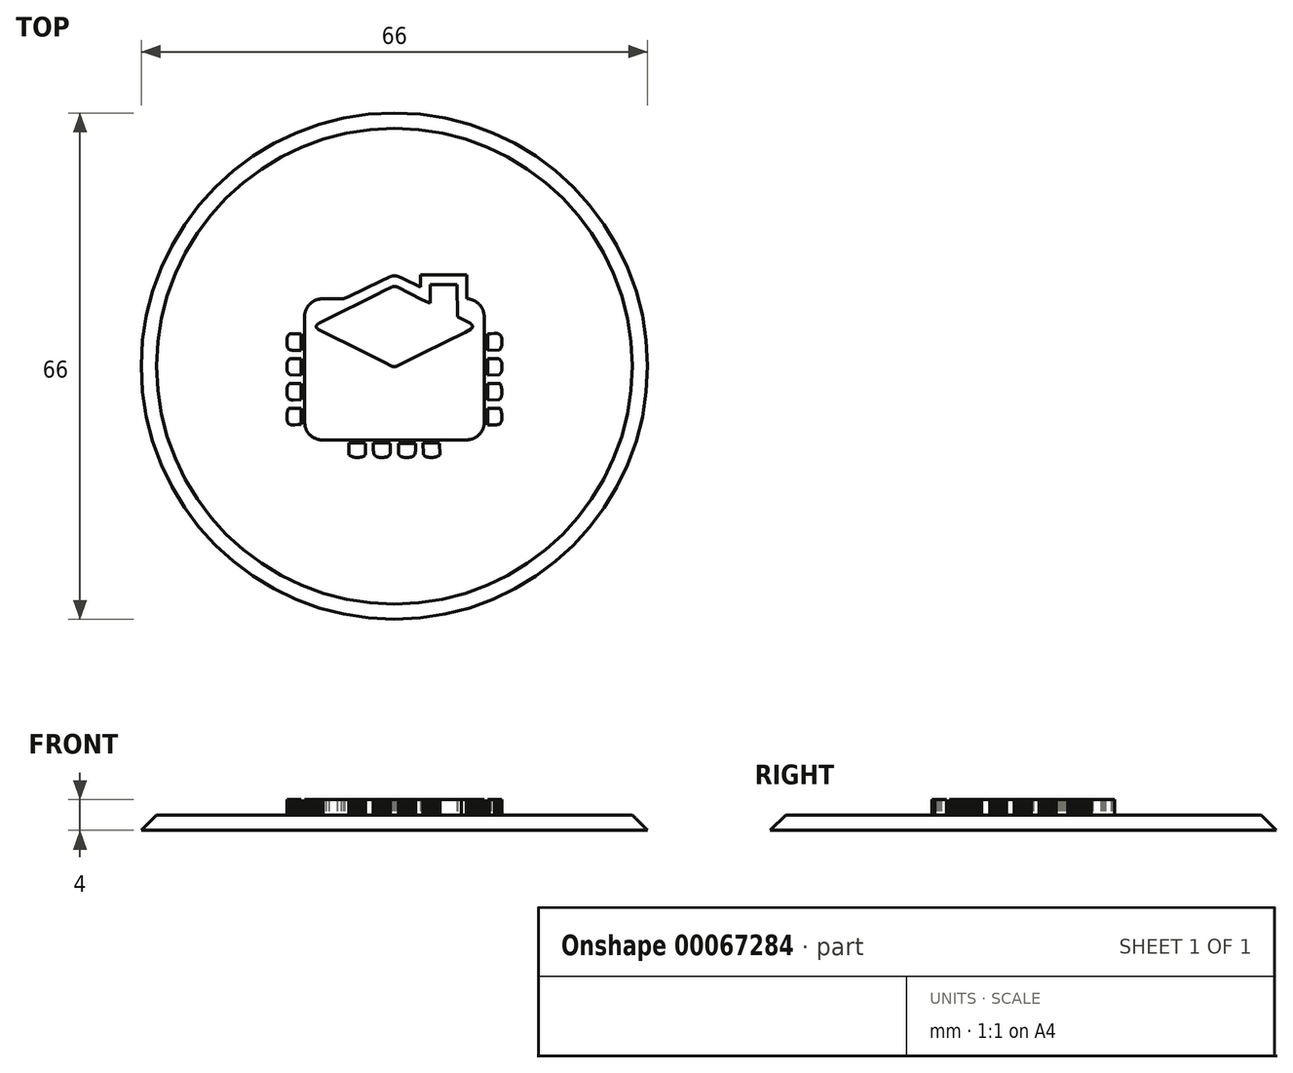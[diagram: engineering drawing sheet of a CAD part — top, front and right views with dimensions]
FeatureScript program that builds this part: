
annotation { "Feature Type Name" : "Feature", "Feature Type Description" : "" }
export const myFeature = defineFeature(function(context is Context, id is Id, definition is map)
    precondition{}
    {
        {
            var Q0;
            Q0=qCreatedBy(makeId("Top.planeOp"),FACE);
            var sketch = newSketch(context, id + "F0", { "sketchPlane" : qUnion([Q0])});
            skCircle(sketch, "E0", {"center": v(0, 0) * mm, "radius": 33 * mm});
            skSolve(sketch);
        }
        {
            var Q0;
            Q0 = qSketchRegion(id + "F0", true);
            extrude(context, id + "F1", {"entities" : qUnion([Q0]), "depth" : 2 * mm, "hasDraft" : true, "draftAngle" : 45 * degree, "draftPullDirection" : true});
        }
        {
            var Q0;
            Q0=qCreatedBy(makeId("Top.planeOp"),FACE);
            var sketch = newSketch(context, id + "F2", { "sketchPlane" : qUnion([Q0])});
            skLineSegment(sketch, "E1", {"start": v(3.39, 11.92) * mm, "end": v(9.43, 11.9) * mm});
            skLineSegment(sketch, "E2", {"start": v(9.43, 11.9) * mm, "end": v(9.45, 8.81) * mm});
            skLineSegment(sketch, "E3", {"start": v(9.45, 8.81) * mm, "end": v(9.52, 8.8) * mm});
            skLineSegment(sketch, "E4", {"start": v(9.52, 8.8) * mm, "end": v(9.6, 8.8) * mm});
            skLineSegment(sketch, "E5", {"start": v(9.6, 8.8) * mm, "end": v(9.66, 8.78) * mm});
            skLineSegment(sketch, "E6", {"start": v(9.66, 8.78) * mm, "end": v(9.73, 8.77) * mm});
            skLineSegment(sketch, "E7", {"start": v(9.73, 8.77) * mm, "end": v(9.8, 8.75) * mm});
            skLineSegment(sketch, "E8", {"start": v(9.8, 8.75) * mm, "end": v(9.88, 8.73) * mm});
            skLineSegment(sketch, "E9", {"start": v(9.88, 8.73) * mm, "end": v(9.95, 8.71) * mm});
            skLineSegment(sketch, "E10", {"start": v(9.95, 8.71) * mm, "end": v(10.02, 8.7) * mm});
            skLineSegment(sketch, "E11", {"start": v(10.02, 8.7) * mm, "end": v(10.08, 8.67) * mm});
            skLineSegment(sketch, "E12", {"start": v(10.08, 8.67) * mm, "end": v(10.15, 8.64) * mm});
            skLineSegment(sketch, "E13", {"start": v(10.15, 8.64) * mm, "end": v(10.22, 8.62) * mm});
            skLineSegment(sketch, "E14", {"start": v(10.22, 8.62) * mm, "end": v(10.29, 8.59) * mm});
            skLineSegment(sketch, "E15", {"start": v(10.29, 8.59) * mm, "end": v(10.35, 8.56) * mm});
            skLineSegment(sketch, "E16", {"start": v(10.35, 8.56) * mm, "end": v(10.42, 8.53) * mm});
            skLineSegment(sketch, "E17", {"start": v(10.42, 8.53) * mm, "end": v(10.48, 8.5) * mm});
            skLineSegment(sketch, "E18", {"start": v(10.48, 8.5) * mm, "end": v(10.55, 8.46) * mm});
            skLineSegment(sketch, "E19", {"start": v(10.55, 8.46) * mm, "end": v(10.6, 8.42) * mm});
            skLineSegment(sketch, "E20", {"start": v(10.6, 8.42) * mm, "end": v(10.67, 8.38) * mm});
            skLineSegment(sketch, "E21", {"start": v(10.67, 8.38) * mm, "end": v(10.73, 8.34) * mm});
            skLineSegment(sketch, "E22", {"start": v(10.73, 8.34) * mm, "end": v(10.79, 8.3) * mm});
            skLineSegment(sketch, "E23", {"start": v(10.79, 8.3) * mm, "end": v(10.85, 8.26) * mm});
            skLineSegment(sketch, "E24", {"start": v(10.85, 8.26) * mm, "end": v(10.9, 8.2) * mm});
            skLineSegment(sketch, "E25", {"start": v(10.9, 8.2) * mm, "end": v(10.95, 8.16) * mm});
            skLineSegment(sketch, "E26", {"start": v(10.95, 8.16) * mm, "end": v(11, 8.11) * mm});
            skLineSegment(sketch, "E27", {"start": v(11, 8.11) * mm, "end": v(11.06, 8.06) * mm});
            skLineSegment(sketch, "E28", {"start": v(11.06, 8.06) * mm, "end": v(11.1, 8) * mm});
            skLineSegment(sketch, "E29", {"start": v(11.1, 8) * mm, "end": v(11.15, 7.95) * mm});
            skLineSegment(sketch, "E30", {"start": v(11.15, 7.95) * mm, "end": v(11.2, 7.9) * mm});
            skLineSegment(sketch, "E31", {"start": v(11.2, 7.9) * mm, "end": v(11.24, 7.83) * mm});
            skLineSegment(sketch, "E32", {"start": v(11.24, 7.83) * mm, "end": v(11.29, 7.78) * mm});
            skLineSegment(sketch, "E33", {"start": v(11.29, 7.78) * mm, "end": v(11.33, 7.72) * mm});
            skLineSegment(sketch, "E34", {"start": v(11.33, 7.72) * mm, "end": v(11.37, 7.65) * mm});
            skLineSegment(sketch, "E35", {"start": v(11.37, 7.65) * mm, "end": v(11.41, 7.6) * mm});
            skLineSegment(sketch, "E36", {"start": v(11.41, 7.6) * mm, "end": v(11.45, 7.53) * mm});
            skLineSegment(sketch, "E37", {"start": v(11.45, 7.53) * mm, "end": v(11.48, 7.46) * mm});
            skLineSegment(sketch, "E38", {"start": v(11.48, 7.46) * mm, "end": v(11.5, 7.4) * mm});
            skLineSegment(sketch, "E39", {"start": v(11.5, 7.4) * mm, "end": v(11.53, 7.33) * mm});
            skLineSegment(sketch, "E40", {"start": v(11.53, 7.33) * mm, "end": v(11.56, 7.26) * mm});
            skLineSegment(sketch, "E41", {"start": v(11.56, 7.26) * mm, "end": v(11.58, 7.19) * mm});
            skLineSegment(sketch, "E42", {"start": v(11.58, 7.19) * mm, "end": v(11.6, 7.12) * mm});
            skLineSegment(sketch, "E43", {"start": v(11.6, 7.12) * mm, "end": v(11.62, 7.05) * mm});
            skLineSegment(sketch, "E44", {"start": v(11.62, 7.05) * mm, "end": v(11.64, 6.97) * mm});
            skLineSegment(sketch, "E45", {"start": v(11.64, 6.97) * mm, "end": v(11.65, 6.9) * mm});
            skLineSegment(sketch, "E46", {"start": v(11.65, 6.9) * mm, "end": v(11.67, 6.83) * mm});
            skLineSegment(sketch, "E47", {"start": v(11.67, 6.83) * mm, "end": v(11.68, 6.75) * mm});
            skLineSegment(sketch, "E48", {"start": v(11.68, 6.75) * mm, "end": v(11.69, 6.68) * mm});
            skLineSegment(sketch, "E49", {"start": v(11.69, 6.68) * mm, "end": v(11.7, 6.53) * mm});
            skLineSegment(sketch, "E50", {"start": v(11.7, 6.53) * mm, "end": v(11.72, 6.38) * mm});
            skLineSegment(sketch, "E51", {"start": v(11.72, 6.38) * mm, "end": v(11.72, 6.16) * mm});
            skLineSegment(sketch, "E52", {"start": v(11.72, 6.16) * mm, "end": v(11.73, 5.8) * mm});
            skLineSegment(sketch, "E53", {"start": v(11.73, 5.8) * mm, "end": v(11.72, -7.1) * mm});
            skLineSegment(sketch, "E54", {"start": v(11.72, -7.1) * mm, "end": v(11.73, -7.2) * mm});
            skLineSegment(sketch, "E55", {"start": v(11.73, -7.2) * mm, "end": v(11.73, -7.29) * mm});
            skLineSegment(sketch, "E56", {"start": v(11.73, -7.29) * mm, "end": v(11.72, -7.38) * mm});
            skLineSegment(sketch, "E57", {"start": v(11.72, -7.38) * mm, "end": v(11.72, -7.47) * mm});
            skLineSegment(sketch, "E58", {"start": v(11.72, -7.47) * mm, "end": v(11.7, -7.56) * mm});
            skLineSegment(sketch, "E59", {"start": v(11.7, -7.56) * mm, "end": v(11.69, -7.65) * mm});
            skLineSegment(sketch, "E60", {"start": v(11.69, -7.65) * mm, "end": v(11.67, -7.74) * mm});
            skLineSegment(sketch, "E61", {"start": v(11.67, -7.74) * mm, "end": v(11.65, -7.83) * mm});
            skLineSegment(sketch, "E62", {"start": v(11.65, -7.83) * mm, "end": v(11.63, -7.92) * mm});
            skLineSegment(sketch, "E63", {"start": v(11.63, -7.92) * mm, "end": v(11.6, -8) * mm});
            skLineSegment(sketch, "E64", {"start": v(11.6, -8) * mm, "end": v(11.57, -8.09) * mm});
            skLineSegment(sketch, "E65", {"start": v(11.57, -8.09) * mm, "end": v(11.53, -8.17) * mm});
            skLineSegment(sketch, "E66", {"start": v(11.53, -8.17) * mm, "end": v(11.5, -8.26) * mm});
            skLineSegment(sketch, "E67", {"start": v(11.5, -8.26) * mm, "end": v(11.45, -8.34) * mm});
            skLineSegment(sketch, "E68", {"start": v(11.45, -8.34) * mm, "end": v(11.41, -8.42) * mm});
            skLineSegment(sketch, "E69", {"start": v(11.41, -8.42) * mm, "end": v(11.37, -8.5) * mm});
            skLineSegment(sketch, "E70", {"start": v(11.37, -8.5) * mm, "end": v(11.32, -8.58) * mm});
            skLineSegment(sketch, "E71", {"start": v(11.32, -8.58) * mm, "end": v(11.26, -8.65) * mm});
            skLineSegment(sketch, "E72", {"start": v(11.26, -8.65) * mm, "end": v(11.2, -8.72) * mm});
            skLineSegment(sketch, "E73", {"start": v(11.2, -8.72) * mm, "end": v(11.15, -8.8) * mm});
            skLineSegment(sketch, "E74", {"start": v(11.15, -8.8) * mm, "end": v(11.1, -8.86) * mm});
            skLineSegment(sketch, "E75", {"start": v(11.1, -8.86) * mm, "end": v(11.03, -8.93) * mm});
            skLineSegment(sketch, "E76", {"start": v(11.03, -8.93) * mm, "end": v(10.96, -9) * mm});
            skLineSegment(sketch, "E77", {"start": v(10.96, -9) * mm, "end": v(10.9, -9.05) * mm});
            skLineSegment(sketch, "E78", {"start": v(10.9, -9.05) * mm, "end": v(10.83, -9.11) * mm});
            skLineSegment(sketch, "E79", {"start": v(10.83, -9.11) * mm, "end": v(10.75, -9.17) * mm});
            skLineSegment(sketch, "E80", {"start": v(10.75, -9.17) * mm, "end": v(10.68, -9.22) * mm});
            skLineSegment(sketch, "E81", {"start": v(10.68, -9.22) * mm, "end": v(10.6, -9.27) * mm});
            skLineSegment(sketch, "E82", {"start": v(10.6, -9.27) * mm, "end": v(10.52, -9.32) * mm});
            skLineSegment(sketch, "E83", {"start": v(10.52, -9.32) * mm, "end": v(10.47, -9.35) * mm});
            skLineSegment(sketch, "E84", {"start": v(10.47, -9.35) * mm, "end": v(10.4, -9.38) * mm});
            skLineSegment(sketch, "E85", {"start": v(10.4, -9.38) * mm, "end": v(10.35, -9.4) * mm});
            skLineSegment(sketch, "E86", {"start": v(10.35, -9.4) * mm, "end": v(10.3, -9.43) * mm});
            skLineSegment(sketch, "E87", {"start": v(10.3, -9.43) * mm, "end": v(10.23, -9.45) * mm});
            skLineSegment(sketch, "E88", {"start": v(10.23, -9.45) * mm, "end": v(10.17, -9.47) * mm});
            skLineSegment(sketch, "E89", {"start": v(10.17, -9.47) * mm, "end": v(10.11, -9.5) * mm});
            skLineSegment(sketch, "E90", {"start": v(10.11, -9.5) * mm, "end": v(10.05, -9.51) * mm});
            skLineSegment(sketch, "E91", {"start": v(10.05, -9.51) * mm, "end": v(10, -9.53) * mm});
            skLineSegment(sketch, "E92", {"start": v(10, -9.53) * mm, "end": v(9.93, -9.54) * mm});
            skLineSegment(sketch, "E93", {"start": v(9.93, -9.54) * mm, "end": v(9.87, -9.56) * mm});
            skLineSegment(sketch, "E94", {"start": v(9.87, -9.56) * mm, "end": v(9.8, -9.57) * mm});
            skLineSegment(sketch, "E95", {"start": v(9.8, -9.57) * mm, "end": v(9.68, -9.59) * mm});
            skLineSegment(sketch, "E96", {"start": v(9.68, -9.59) * mm, "end": v(9.55, -9.6) * mm});
            skLineSegment(sketch, "E97", {"start": v(9.55, -9.6) * mm, "end": v(9.36, -9.61) * mm});
            skLineSegment(sketch, "E98", {"start": v(9.36, -9.61) * mm, "end": v(8.73, -9.63) * mm});
            skLineSegment(sketch, "E99", {"start": v(8.73, -9.63) * mm, "end": v(-9.27, -9.62) * mm});
            skLineSegment(sketch, "E100", {"start": v(-9.27, -9.62) * mm, "end": v(-9.38, -9.62) * mm});
            skLineSegment(sketch, "E101", {"start": v(-9.38, -9.62) * mm, "end": v(-9.48, -9.62) * mm});
            skLineSegment(sketch, "E102", {"start": v(-9.48, -9.62) * mm, "end": v(-9.59, -9.61) * mm});
            skLineSegment(sketch, "E103", {"start": v(-9.59, -9.61) * mm, "end": v(-9.69, -9.6) * mm});
            skLineSegment(sketch, "E104", {"start": v(-9.69, -9.6) * mm, "end": v(-9.8, -9.58) * mm});
            skLineSegment(sketch, "E105", {"start": v(-9.8, -9.58) * mm, "end": v(-9.9, -9.56) * mm});
            skLineSegment(sketch, "E106", {"start": v(-9.9, -9.56) * mm, "end": v(-10, -9.54) * mm});
            skLineSegment(sketch, "E107", {"start": v(-10, -9.54) * mm, "end": v(-10.1, -9.5) * mm});
            skLineSegment(sketch, "E108", {"start": v(-10.1, -9.5) * mm, "end": v(-10.19, -9.47) * mm});
            skLineSegment(sketch, "E109", {"start": v(-10.19, -9.47) * mm, "end": v(-10.28, -9.43) * mm});
            skLineSegment(sketch, "E110", {"start": v(-10.28, -9.43) * mm, "end": v(-10.38, -9.39) * mm});
            skLineSegment(sketch, "E111", {"start": v(-10.38, -9.39) * mm, "end": v(-10.47, -9.34) * mm});
            skLineSegment(sketch, "E112", {"start": v(-10.47, -9.34) * mm, "end": v(-10.56, -9.3) * mm});
            skLineSegment(sketch, "E113", {"start": v(-10.56, -9.3) * mm, "end": v(-10.65, -9.24) * mm});
            skLineSegment(sketch, "E114", {"start": v(-10.65, -9.24) * mm, "end": v(-10.73, -9.18) * mm});
            skLineSegment(sketch, "E115", {"start": v(-10.73, -9.18) * mm, "end": v(-10.82, -9.12) * mm});
            skLineSegment(sketch, "E116", {"start": v(-10.82, -9.12) * mm, "end": v(-10.9, -9.05) * mm});
            skLineSegment(sketch, "E117", {"start": v(-10.9, -9.05) * mm, "end": v(-10.98, -8.98) * mm});
            skLineSegment(sketch, "E118", {"start": v(-10.98, -8.98) * mm, "end": v(-11.05, -8.91) * mm});
            skLineSegment(sketch, "E119", {"start": v(-11.05, -8.91) * mm, "end": v(-11.12, -8.84) * mm});
            skLineSegment(sketch, "E120", {"start": v(-11.12, -8.84) * mm, "end": v(-11.19, -8.76) * mm});
            skLineSegment(sketch, "E121", {"start": v(-11.19, -8.76) * mm, "end": v(-11.25, -8.68) * mm});
            skLineSegment(sketch, "E122", {"start": v(-11.25, -8.68) * mm, "end": v(-11.31, -8.6) * mm});
            skLineSegment(sketch, "E123", {"start": v(-11.31, -8.6) * mm, "end": v(-11.37, -8.51) * mm});
            skLineSegment(sketch, "E124", {"start": v(-11.37, -8.51) * mm, "end": v(-11.42, -8.42) * mm});
            skLineSegment(sketch, "E125", {"start": v(-11.42, -8.42) * mm, "end": v(-11.47, -8.33) * mm});
            skLineSegment(sketch, "E126", {"start": v(-11.47, -8.33) * mm, "end": v(-11.52, -8.24) * mm});
            skLineSegment(sketch, "E127", {"start": v(-11.52, -8.24) * mm, "end": v(-11.56, -8.14) * mm});
            skLineSegment(sketch, "E128", {"start": v(-11.56, -8.14) * mm, "end": v(-11.6, -8.04) * mm});
            skLineSegment(sketch, "E129", {"start": v(-11.6, -8.04) * mm, "end": v(-11.62, -7.95) * mm});
            skLineSegment(sketch, "E130", {"start": v(-11.62, -7.95) * mm, "end": v(-11.65, -7.8) * mm});
            skLineSegment(sketch, "E131", {"start": v(-11.65, -7.8) * mm, "end": v(-11.68, -7.66) * mm});
            skLineSegment(sketch, "E132", {"start": v(-11.68, -7.66) * mm, "end": v(-11.7, -7.41) * mm});
            skLineSegment(sketch, "E133", {"start": v(-11.7, -7.41) * mm, "end": v(-11.73, -6.62) * mm});
            skLineSegment(sketch, "E134", {"start": v(-11.73, -6.62) * mm, "end": v(-11.74, 5.68) * mm});
            skLineSegment(sketch, "E135", {"start": v(-11.74, 5.68) * mm, "end": v(-11.72, 6.43) * mm});
            skLineSegment(sketch, "E136", {"start": v(-11.72, 6.43) * mm, "end": v(-11.7, 6.62) * mm});
            skLineSegment(sketch, "E137", {"start": v(-11.7, 6.62) * mm, "end": v(-11.7, 6.75) * mm});
            skLineSegment(sketch, "E138", {"start": v(-11.7, 6.75) * mm, "end": v(-11.68, 6.8) * mm});
            skLineSegment(sketch, "E139", {"start": v(-11.68, 6.8) * mm, "end": v(-11.67, 6.87) * mm});
            skLineSegment(sketch, "E140", {"start": v(-11.67, 6.87) * mm, "end": v(-11.66, 6.93) * mm});
            skLineSegment(sketch, "E141", {"start": v(-11.66, 6.93) * mm, "end": v(-11.65, 7) * mm});
            skLineSegment(sketch, "E142", {"start": v(-11.65, 7) * mm, "end": v(-11.63, 7.05) * mm});
            skLineSegment(sketch, "E143", {"start": v(-11.63, 7.05) * mm, "end": v(-11.62, 7.11) * mm});
            skLineSegment(sketch, "E144", {"start": v(-11.62, 7.11) * mm, "end": v(-11.6, 7.17) * mm});
            skLineSegment(sketch, "E145", {"start": v(-11.6, 7.17) * mm, "end": v(-11.58, 7.23) * mm});
            skLineSegment(sketch, "E146", {"start": v(-11.58, 7.23) * mm, "end": v(-11.56, 7.3) * mm});
            skLineSegment(sketch, "E147", {"start": v(-11.56, 7.3) * mm, "end": v(-11.53, 7.35) * mm});
            skLineSegment(sketch, "E148", {"start": v(-11.53, 7.35) * mm, "end": v(-11.5, 7.4) * mm});
            skLineSegment(sketch, "E149", {"start": v(-11.5, 7.4) * mm, "end": v(-11.48, 7.46) * mm});
            skLineSegment(sketch, "E150", {"start": v(-11.48, 7.46) * mm, "end": v(-11.44, 7.53) * mm});
            skLineSegment(sketch, "E151", {"start": v(-11.44, 7.53) * mm, "end": v(-11.4, 7.6) * mm});
            skLineSegment(sketch, "E152", {"start": v(-11.4, 7.6) * mm, "end": v(-11.36, 7.67) * mm});
            skLineSegment(sketch, "E153", {"start": v(-11.36, 7.67) * mm, "end": v(-11.32, 7.74) * mm});
            skLineSegment(sketch, "E154", {"start": v(-11.32, 7.74) * mm, "end": v(-11.27, 7.8) * mm});
            skLineSegment(sketch, "E155", {"start": v(-11.27, 7.8) * mm, "end": v(-11.22, 7.87) * mm});
            skLineSegment(sketch, "E156", {"start": v(-11.22, 7.87) * mm, "end": v(-11.17, 7.94) * mm});
            skLineSegment(sketch, "E157", {"start": v(-11.17, 7.94) * mm, "end": v(-11.12, 8) * mm});
            skLineSegment(sketch, "E158", {"start": v(-11.12, 8) * mm, "end": v(-11.06, 8.06) * mm});
            skLineSegment(sketch, "E159", {"start": v(-11.06, 8.06) * mm, "end": v(-11, 8.11) * mm});
            skLineSegment(sketch, "E160", {"start": v(-11, 8.11) * mm, "end": v(-10.95, 8.17) * mm});
            skLineSegment(sketch, "E161", {"start": v(-10.95, 8.17) * mm, "end": v(-10.89, 8.22) * mm});
            skLineSegment(sketch, "E162", {"start": v(-10.89, 8.22) * mm, "end": v(-10.83, 8.27) * mm});
            skLineSegment(sketch, "E163", {"start": v(-10.83, 8.27) * mm, "end": v(-10.76, 8.32) * mm});
            skLineSegment(sketch, "E164", {"start": v(-10.76, 8.32) * mm, "end": v(-10.7, 8.37) * mm});
            skLineSegment(sketch, "E165", {"start": v(-10.7, 8.37) * mm, "end": v(-10.63, 8.42) * mm});
            skLineSegment(sketch, "E166", {"start": v(-10.63, 8.42) * mm, "end": v(-10.56, 8.46) * mm});
            skLineSegment(sketch, "E167", {"start": v(-10.56, 8.46) * mm, "end": v(-10.5, 8.5) * mm});
            skLineSegment(sketch, "E168", {"start": v(-10.5, 8.5) * mm, "end": v(-10.42, 8.54) * mm});
            skLineSegment(sketch, "E169", {"start": v(-10.42, 8.54) * mm, "end": v(-10.35, 8.57) * mm});
            skLineSegment(sketch, "E170", {"start": v(-10.35, 8.57) * mm, "end": v(-10.28, 8.6) * mm});
            skLineSegment(sketch, "E171", {"start": v(-10.28, 8.6) * mm, "end": v(-10.2, 8.63) * mm});
            skLineSegment(sketch, "E172", {"start": v(-10.2, 8.63) * mm, "end": v(-10.13, 8.66) * mm});
            skLineSegment(sketch, "E173", {"start": v(-10.13, 8.66) * mm, "end": v(-10.05, 8.68) * mm});
            skLineSegment(sketch, "E174", {"start": v(-10.05, 8.68) * mm, "end": v(-9.97, 8.7) * mm});
            skLineSegment(sketch, "E175", {"start": v(-9.97, 8.7) * mm, "end": v(-9.9, 8.72) * mm});
            skLineSegment(sketch, "E176", {"start": v(-9.9, 8.72) * mm, "end": v(-9.81, 8.74) * mm});
            skLineSegment(sketch, "E177", {"start": v(-9.81, 8.74) * mm, "end": v(-9.73, 8.75) * mm});
            skLineSegment(sketch, "E178", {"start": v(-9.73, 8.75) * mm, "end": v(-9.65, 8.76) * mm});
            skLineSegment(sketch, "E179", {"start": v(-9.65, 8.76) * mm, "end": v(-9.44, 8.77) * mm});
            skLineSegment(sketch, "E180", {"start": v(-9.44, 8.77) * mm, "end": v(-9.24, 8.79) * mm});
            skLineSegment(sketch, "E181", {"start": v(-9.24, 8.79) * mm, "end": v(-8.92, 8.8) * mm});
            skLineSegment(sketch, "E182", {"start": v(-8.92, 8.8) * mm, "end": v(-7.46, 8.79) * mm});
            skLineSegment(sketch, "E183", {"start": v(-7.46, 8.79) * mm, "end": v(-6.94, 8.8) * mm});
            skLineSegment(sketch, "E184", {"start": v(-6.94, 8.8) * mm, "end": v(-6.63, 8.8) * mm});
            skLineSegment(sketch, "E185", {"start": v(-6.63, 8.8) * mm, "end": v(-6.5, 8.83) * mm});
            skLineSegment(sketch, "E186", {"start": v(-6.5, 8.83) * mm, "end": v(-6.03, 9.03) * mm});
            skLineSegment(sketch, "E187", {"start": v(-6.03, 9.03) * mm, "end": v(-1.65, 11.14) * mm});
            skLineSegment(sketch, "E188", {"start": v(-1.65, 11.14) * mm, "end": v(-0.7, 11.6) * mm});
            skLineSegment(sketch, "E189", {"start": v(-0.7, 11.6) * mm, "end": v(-0.5, 11.68) * mm});
            skLineSegment(sketch, "E190", {"start": v(-0.5, 11.68) * mm, "end": v(-0.36, 11.74) * mm});
            skLineSegment(sketch, "E191", {"start": v(-0.36, 11.74) * mm, "end": v(-0.25, 11.77) * mm});
            skLineSegment(sketch, "E192", {"start": v(-0.25, 11.77) * mm, "end": v(-0.2, 11.77) * mm});
            skLineSegment(sketch, "E193", {"start": v(-0.2, 11.77) * mm, "end": v(-0.16, 11.78) * mm});
            skLineSegment(sketch, "E194", {"start": v(-0.16, 11.78) * mm, "end": v(-0.11, 11.79) * mm});
            skLineSegment(sketch, "E195", {"start": v(-0.11, 11.79) * mm, "end": v(-0.06, 11.8) * mm});
            skLineSegment(sketch, "E196", {"start": v(-0.06, 11.8) * mm, "end": v(-0.02, 11.8) * mm});
            skLineSegment(sketch, "E197", {"start": v(-0.02, 11.8) * mm, "end": v(0.03, 11.8) * mm});
            skLineSegment(sketch, "E198", {"start": v(0.03, 11.8) * mm, "end": v(0.08, 11.79) * mm});
            skLineSegment(sketch, "E199", {"start": v(0.08, 11.79) * mm, "end": v(0.12, 11.78) * mm});
            skLineSegment(sketch, "E200", {"start": v(0.12, 11.78) * mm, "end": v(0.17, 11.78) * mm});
            skLineSegment(sketch, "E201", {"start": v(0.17, 11.78) * mm, "end": v(0.22, 11.77) * mm});
            skLineSegment(sketch, "E202", {"start": v(0.22, 11.77) * mm, "end": v(0.26, 11.76) * mm});
            skLineSegment(sketch, "E203", {"start": v(0.26, 11.76) * mm, "end": v(0.35, 11.73) * mm});
            skLineSegment(sketch, "E204", {"start": v(0.35, 11.73) * mm, "end": v(0.44, 11.7) * mm});
            skLineSegment(sketch, "E205", {"start": v(0.44, 11.7) * mm, "end": v(0.58, 11.66) * mm});
            skLineSegment(sketch, "E206", {"start": v(0.58, 11.66) * mm, "end": v(1.05, 11.44) * mm});
            skLineSegment(sketch, "E207", {"start": v(1.05, 11.44) * mm, "end": v(3.39, 10.3) * mm});
            skLineSegment(sketch, "E208", {"start": v(3.39, 10.3) * mm, "end": v(3.39, 11.92) * mm});
            skLineSegment(sketch, "E209", {"start": v(4.65, 10.66) * mm, "end": v(4.64, 8.2) * mm});
            skLineSegment(sketch, "E210", {"start": v(4.64, 8.2) * mm, "end": v(4.5, 8.26) * mm});
            skLineSegment(sketch, "E211", {"start": v(4.5, 8.26) * mm, "end": v(3.6, 8.68) * mm});
            skLineSegment(sketch, "E212", {"start": v(3.6, 8.68) * mm, "end": v(0.39, 10.3) * mm});
            skLineSegment(sketch, "E213", {"start": v(0.39, 10.3) * mm, "end": v(0.35, 10.32) * mm});
            skLineSegment(sketch, "E214", {"start": v(0.35, 10.32) * mm, "end": v(0.3, 10.34) * mm});
            skLineSegment(sketch, "E215", {"start": v(0.3, 10.34) * mm, "end": v(0.27, 10.35) * mm});
            skLineSegment(sketch, "E216", {"start": v(0.27, 10.35) * mm, "end": v(0.23, 10.37) * mm});
            skLineSegment(sketch, "E217", {"start": v(0.23, 10.37) * mm, "end": v(0.19, 10.38) * mm});
            skLineSegment(sketch, "E218", {"start": v(0.19, 10.38) * mm, "end": v(0.15, 10.39) * mm});
            skLineSegment(sketch, "E219", {"start": v(0.15, 10.39) * mm, "end": v(0.1, 10.4) * mm});
            skLineSegment(sketch, "E220", {"start": v(0.1, 10.4) * mm, "end": v(0.07, 10.4) * mm});
            skLineSegment(sketch, "E221", {"start": v(0.07, 10.4) * mm, "end": v(0.03, 10.4) * mm});
            skLineSegment(sketch, "E222", {"start": v(0.03, 10.4) * mm, "end": v(-0.02, 10.4) * mm});
            skLineSegment(sketch, "E223", {"start": v(-0.02, 10.4) * mm, "end": v(-0.06, 10.4) * mm});
            skLineSegment(sketch, "E224", {"start": v(-0.06, 10.4) * mm, "end": v(-0.1, 10.39) * mm});
            skLineSegment(sketch, "E225", {"start": v(-0.1, 10.39) * mm, "end": v(-0.14, 10.38) * mm});
            skLineSegment(sketch, "E226", {"start": v(-0.14, 10.38) * mm, "end": v(-0.18, 10.37) * mm});
            skLineSegment(sketch, "E227", {"start": v(-0.18, 10.37) * mm, "end": v(-0.22, 10.36) * mm});
            skLineSegment(sketch, "E228", {"start": v(-0.22, 10.36) * mm, "end": v(-0.26, 10.35) * mm});
            skLineSegment(sketch, "E229", {"start": v(-0.26, 10.35) * mm, "end": v(-0.34, 10.32) * mm});
            skLineSegment(sketch, "E230", {"start": v(-0.34, 10.32) * mm, "end": v(-0.46, 10.27) * mm});
            skLineSegment(sketch, "E231", {"start": v(-0.46, 10.27) * mm, "end": v(-0.76, 10.12) * mm});
            skLineSegment(sketch, "E232", {"start": v(-0.76, 10.12) * mm, "end": v(-1.07, 9.96) * mm});
            skLineSegment(sketch, "E233", {"start": v(-1.07, 9.96) * mm, "end": v(-2.62, 9.18) * mm});
            skLineSegment(sketch, "E234", {"start": v(-2.62, 9.18) * mm, "end": v(-8.57, 6.24) * mm});
            skLineSegment(sketch, "E235", {"start": v(-8.57, 6.24) * mm, "end": v(-9.81, 5.61) * mm});
            skLineSegment(sketch, "E236", {"start": v(-9.81, 5.61) * mm, "end": v(-9.88, 5.58) * mm});
            skLineSegment(sketch, "E237", {"start": v(-9.88, 5.58) * mm, "end": v(-9.95, 5.54) * mm});
            skLineSegment(sketch, "E238", {"start": v(-9.95, 5.54) * mm, "end": v(-10, 5.5) * mm});
            skLineSegment(sketch, "E239", {"start": v(-10, 5.5) * mm, "end": v(-10.05, 5.46) * mm});
            skLineSegment(sketch, "E240", {"start": v(-10.05, 5.46) * mm, "end": v(-10.08, 5.42) * mm});
            skLineSegment(sketch, "E241", {"start": v(-10.08, 5.42) * mm, "end": v(-10.11, 5.38) * mm});
            skLineSegment(sketch, "E242", {"start": v(-10.11, 5.38) * mm, "end": v(-10.13, 5.36) * mm});
            skLineSegment(sketch, "E243", {"start": v(-10.13, 5.36) * mm, "end": v(-10.14, 5.34) * mm});
            skLineSegment(sketch, "E244", {"start": v(-10.14, 5.34) * mm, "end": v(-10.15, 5.32) * mm});
            skLineSegment(sketch, "E245", {"start": v(-10.15, 5.32) * mm, "end": v(-10.16, 5.3) * mm});
            skLineSegment(sketch, "E246", {"start": v(-10.16, 5.3) * mm, "end": v(-10.17, 5.27) * mm});
            skLineSegment(sketch, "E247", {"start": v(-10.17, 5.27) * mm, "end": v(-10.17, 5.25) * mm});
            skLineSegment(sketch, "E248", {"start": v(-10.17, 5.25) * mm, "end": v(-10.18, 5.22) * mm});
            skLineSegment(sketch, "E249", {"start": v(-10.18, 5.22) * mm, "end": v(-10.18, 5.2) * mm});
            skLineSegment(sketch, "E250", {"start": v(-10.18, 5.2) * mm, "end": v(-10.18, 5.17) * mm});
            skLineSegment(sketch, "E251", {"start": v(-10.18, 5.17) * mm, "end": v(-10.18, 5.15) * mm});
            skLineSegment(sketch, "E252", {"start": v(-10.18, 5.15) * mm, "end": v(-10.18, 5.12) * mm});
            skLineSegment(sketch, "E253", {"start": v(-10.18, 5.12) * mm, "end": v(-10.17, 5.1) * mm});
            skLineSegment(sketch, "E254", {"start": v(-10.17, 5.1) * mm, "end": v(-10.16, 5.07) * mm});
            skLineSegment(sketch, "E255", {"start": v(-10.16, 5.07) * mm, "end": v(-10.15, 5.04) * mm});
            skLineSegment(sketch, "E256", {"start": v(-10.15, 5.04) * mm, "end": v(-10.14, 5.01) * mm});
            skLineSegment(sketch, "E257", {"start": v(-10.14, 5.01) * mm, "end": v(-10.13, 4.99) * mm});
            skLineSegment(sketch, "E258", {"start": v(-10.13, 4.99) * mm, "end": v(-10.12, 4.97) * mm});
            skLineSegment(sketch, "E259", {"start": v(-10.12, 4.97) * mm, "end": v(-10.1, 4.94) * mm});
            skLineSegment(sketch, "E260", {"start": v(-10.1, 4.94) * mm, "end": v(-10.1, 4.92) * mm});
            skLineSegment(sketch, "E261", {"start": v(-10.1, 4.92) * mm, "end": v(-10.08, 4.9) * mm});
            skLineSegment(sketch, "E262", {"start": v(-10.08, 4.9) * mm, "end": v(-10.04, 4.87) * mm});
            skLineSegment(sketch, "E263", {"start": v(-10.04, 4.87) * mm, "end": v(-10, 4.83) * mm});
            skLineSegment(sketch, "E264", {"start": v(-10, 4.83) * mm, "end": v(-9.96, 4.8) * mm});
            skLineSegment(sketch, "E265", {"start": v(-9.96, 4.8) * mm, "end": v(-9.8, 4.71) * mm});
            skLineSegment(sketch, "E266", {"start": v(-9.8, 4.71) * mm, "end": v(-9.58, 4.6) * mm});
            skLineSegment(sketch, "E267", {"start": v(-9.58, 4.6) * mm, "end": v(-4.3, 1.96) * mm});
            skLineSegment(sketch, "E268", {"start": v(-4.3, 1.96) * mm, "end": v(-2.91, 1.3) * mm});
            skLineSegment(sketch, "E269", {"start": v(-2.91, 1.3) * mm, "end": v(-1.37, 0.52) * mm});
            skLineSegment(sketch, "E270", {"start": v(-1.37, 0.52) * mm, "end": v(-0.27, -0.01) * mm});
            skLineSegment(sketch, "E271", {"start": v(-0.27, -0.01) * mm, "end": v(-0.24, -0.03) * mm});
            skLineSegment(sketch, "E272", {"start": v(-0.24, -0.03) * mm, "end": v(-0.22, -0.04) * mm});
            skLineSegment(sketch, "E273", {"start": v(-0.22, -0.04) * mm, "end": v(-0.19, -0.05) * mm});
            skLineSegment(sketch, "E274", {"start": v(-0.19, -0.05) * mm, "end": v(-0.16, -0.06) * mm});
            skLineSegment(sketch, "E275", {"start": v(-0.16, -0.06) * mm, "end": v(-0.14, -0.06) * mm});
            skLineSegment(sketch, "E276", {"start": v(-0.14, -0.06) * mm, "end": v(-0.1, -0.07) * mm});
            skLineSegment(sketch, "E277", {"start": v(-0.1, -0.07) * mm, "end": v(-0.08, -0.07) * mm});
            skLineSegment(sketch, "E278", {"start": v(-0.08, -0.07) * mm, "end": v(-0.05, -0.07) * mm});
            skLineSegment(sketch, "E279", {"start": v(-0.05, -0.07) * mm, "end": v(-0.03, -0.07) * mm});
            skLineSegment(sketch, "E280", {"start": v(-0.03, -0.07) * mm, "end": v(0.03, -0.07) * mm});
            skLineSegment(sketch, "E281", {"start": v(0.03, -0.07) * mm, "end": v(0.08, -0.06) * mm});
            skLineSegment(sketch, "E282", {"start": v(0.08, -0.06) * mm, "end": v(0.14, -0.05) * mm});
            skLineSegment(sketch, "E283", {"start": v(0.14, -0.05) * mm, "end": v(0.25, -0.02) * mm});
            skLineSegment(sketch, "E284", {"start": v(0.25, -0.02) * mm, "end": v(0.5, 0.1) * mm});
            skLineSegment(sketch, "E285", {"start": v(0.5, 0.1) * mm, "end": v(3.8, 1.72) * mm});
            skLineSegment(sketch, "E286", {"start": v(3.8, 1.72) * mm, "end": v(9.2, 4.41) * mm});
            skLineSegment(sketch, "E287", {"start": v(9.2, 4.41) * mm, "end": v(10.03, 4.86) * mm});
            skLineSegment(sketch, "E288", {"start": v(10.03, 4.86) * mm, "end": v(10.04, 4.87) * mm});
            skLineSegment(sketch, "E289", {"start": v(10.04, 4.87) * mm, "end": v(10.06, 4.9) * mm});
            skLineSegment(sketch, "E290", {"start": v(10.06, 4.9) * mm, "end": v(10.08, 4.9) * mm});
            skLineSegment(sketch, "E291", {"start": v(10.08, 4.9) * mm, "end": v(10.1, 4.93) * mm});
            skLineSegment(sketch, "E292", {"start": v(10.1, 4.93) * mm, "end": v(10.1, 4.95) * mm});
            skLineSegment(sketch, "E293", {"start": v(10.1, 4.95) * mm, "end": v(10.12, 4.97) * mm});
            skLineSegment(sketch, "E294", {"start": v(10.12, 4.97) * mm, "end": v(10.13, 4.99) * mm});
            skLineSegment(sketch, "E295", {"start": v(10.13, 4.99) * mm, "end": v(10.14, 5.01) * mm});
            skLineSegment(sketch, "E296", {"start": v(10.14, 5.01) * mm, "end": v(10.15, 5.03) * mm});
            skLineSegment(sketch, "E297", {"start": v(10.15, 5.03) * mm, "end": v(10.15, 5.06) * mm});
            skLineSegment(sketch, "E298", {"start": v(10.15, 5.06) * mm, "end": v(10.16, 5.08) * mm});
            skLineSegment(sketch, "E299", {"start": v(10.16, 5.08) * mm, "end": v(10.16, 5.1) * mm});
            skLineSegment(sketch, "E300", {"start": v(10.16, 5.1) * mm, "end": v(10.17, 5.13) * mm});
            skLineSegment(sketch, "E301", {"start": v(10.17, 5.13) * mm, "end": v(10.17, 5.15) * mm});
            skLineSegment(sketch, "E302", {"start": v(10.17, 5.15) * mm, "end": v(10.17, 5.2) * mm});
            skLineSegment(sketch, "E303", {"start": v(10.17, 5.2) * mm, "end": v(10.16, 5.23) * mm});
            skLineSegment(sketch, "E304", {"start": v(10.16, 5.23) * mm, "end": v(10.16, 5.25) * mm});
            skLineSegment(sketch, "E305", {"start": v(10.16, 5.25) * mm, "end": v(10.15, 5.28) * mm});
            skLineSegment(sketch, "E306", {"start": v(10.15, 5.28) * mm, "end": v(10.15, 5.3) * mm});
            skLineSegment(sketch, "E307", {"start": v(10.15, 5.3) * mm, "end": v(10.14, 5.32) * mm});
            skLineSegment(sketch, "E308", {"start": v(10.14, 5.32) * mm, "end": v(10.13, 5.34) * mm});
            skLineSegment(sketch, "E309", {"start": v(10.13, 5.34) * mm, "end": v(10.12, 5.37) * mm});
            skLineSegment(sketch, "E310", {"start": v(10.12, 5.37) * mm, "end": v(10.1, 5.39) * mm});
            skLineSegment(sketch, "E311", {"start": v(10.1, 5.39) * mm, "end": v(10.1, 5.4) * mm});
            skLineSegment(sketch, "E312", {"start": v(10.1, 5.4) * mm, "end": v(10.08, 5.42) * mm});
            skLineSegment(sketch, "E313", {"start": v(10.08, 5.42) * mm, "end": v(10.06, 5.44) * mm});
            skLineSegment(sketch, "E314", {"start": v(10.06, 5.44) * mm, "end": v(10.04, 5.46) * mm});
            skLineSegment(sketch, "E315", {"start": v(10.04, 5.46) * mm, "end": v(10.03, 5.47) * mm});
            skLineSegment(sketch, "E316", {"start": v(10.03, 5.47) * mm, "end": v(9.84, 5.59) * mm});
            skLineSegment(sketch, "E317", {"start": v(9.84, 5.59) * mm, "end": v(9.6, 5.73) * mm});
            skLineSegment(sketch, "E318", {"start": v(9.6, 5.73) * mm, "end": v(8.2, 6.4) * mm});
            skLineSegment(sketch, "E319", {"start": v(8.2, 6.4) * mm, "end": v(8.19, 10.66) * mm});
            skLineSegment(sketch, "E320", {"start": v(8.19, 10.66) * mm, "end": v(4.65, 10.66) * mm});
            skLineSegment(sketch, "E321", {"start": v(-13.63, 4.2) * mm, "end": v(-12.17, 4.23) * mm});
            skLineSegment(sketch, "E322", {"start": v(-12.17, 4.23) * mm, "end": v(-12.15, 2.07) * mm});
            skLineSegment(sketch, "E323", {"start": v(-12.15, 2.07) * mm, "end": v(-13.3, 2.08) * mm});
            skLineSegment(sketch, "E324", {"start": v(-13.3, 2.08) * mm, "end": v(-13.52, 2.1) * mm});
            skLineSegment(sketch, "E325", {"start": v(-13.52, 2.1) * mm, "end": v(-13.67, 2.12) * mm});
            skLineSegment(sketch, "E326", {"start": v(-13.67, 2.12) * mm, "end": v(-13.7, 2.15) * mm});
            skLineSegment(sketch, "E327", {"start": v(-13.7, 2.15) * mm, "end": v(-13.74, 2.17) * mm});
            skLineSegment(sketch, "E328", {"start": v(-13.74, 2.17) * mm, "end": v(-13.77, 2.2) * mm});
            skLineSegment(sketch, "E329", {"start": v(-13.77, 2.2) * mm, "end": v(-13.8, 2.23) * mm});
            skLineSegment(sketch, "E330", {"start": v(-13.8, 2.23) * mm, "end": v(-13.82, 2.26) * mm});
            skLineSegment(sketch, "E331", {"start": v(-13.82, 2.26) * mm, "end": v(-13.85, 2.3) * mm});
            skLineSegment(sketch, "E332", {"start": v(-13.85, 2.3) * mm, "end": v(-13.87, 2.33) * mm});
            skLineSegment(sketch, "E333", {"start": v(-13.87, 2.33) * mm, "end": v(-13.9, 2.36) * mm});
            skLineSegment(sketch, "E334", {"start": v(-13.9, 2.36) * mm, "end": v(-13.9, 2.4) * mm});
            skLineSegment(sketch, "E335", {"start": v(-13.9, 2.4) * mm, "end": v(-13.92, 2.44) * mm});
            skLineSegment(sketch, "E336", {"start": v(-13.92, 2.44) * mm, "end": v(-13.94, 2.48) * mm});
            skLineSegment(sketch, "E337", {"start": v(-13.94, 2.48) * mm, "end": v(-13.95, 2.52) * mm});
            skLineSegment(sketch, "E338", {"start": v(-13.95, 2.52) * mm, "end": v(-13.96, 2.56) * mm});
            skLineSegment(sketch, "E339", {"start": v(-13.96, 2.56) * mm, "end": v(-13.97, 2.6) * mm});
            skLineSegment(sketch, "E340", {"start": v(-13.97, 2.6) * mm, "end": v(-13.99, 2.68) * mm});
            skLineSegment(sketch, "E341", {"start": v(-13.99, 2.68) * mm, "end": v(-14, 2.76) * mm});
            skLineSegment(sketch, "E342", {"start": v(-14, 2.76) * mm, "end": v(-14.01, 2.93) * mm});
            skLineSegment(sketch, "E343", {"start": v(-14.01, 2.93) * mm, "end": v(-14.02, 3.14) * mm});
            skLineSegment(sketch, "E344", {"start": v(-14.02, 3.14) * mm, "end": v(-14.02, 3.22) * mm});
            skLineSegment(sketch, "E345", {"start": v(-14.02, 3.22) * mm, "end": v(-14.02, 3.33) * mm});
            skLineSegment(sketch, "E346", {"start": v(-14.02, 3.33) * mm, "end": v(-14, 3.48) * mm});
            skLineSegment(sketch, "E347", {"start": v(-14, 3.48) * mm, "end": v(-13.99, 3.6) * mm});
            skLineSegment(sketch, "E348", {"start": v(-13.99, 3.6) * mm, "end": v(-13.98, 3.68) * mm});
            skLineSegment(sketch, "E349", {"start": v(-13.98, 3.68) * mm, "end": v(-13.96, 3.76) * mm});
            skLineSegment(sketch, "E350", {"start": v(-13.96, 3.76) * mm, "end": v(-13.95, 3.8) * mm});
            skLineSegment(sketch, "E351", {"start": v(-13.95, 3.8) * mm, "end": v(-13.93, 3.83) * mm});
            skLineSegment(sketch, "E352", {"start": v(-13.93, 3.83) * mm, "end": v(-13.92, 3.87) * mm});
            skLineSegment(sketch, "E353", {"start": v(-13.92, 3.87) * mm, "end": v(-13.9, 3.9) * mm});
            skLineSegment(sketch, "E354", {"start": v(-13.9, 3.9) * mm, "end": v(-13.89, 3.94) * mm});
            skLineSegment(sketch, "E355", {"start": v(-13.89, 3.94) * mm, "end": v(-13.87, 3.97) * mm});
            skLineSegment(sketch, "E356", {"start": v(-13.87, 3.97) * mm, "end": v(-13.85, 4) * mm});
            skLineSegment(sketch, "E357", {"start": v(-13.85, 4) * mm, "end": v(-13.83, 4.03) * mm});
            skLineSegment(sketch, "E358", {"start": v(-13.83, 4.03) * mm, "end": v(-13.8, 4.06) * mm});
            skLineSegment(sketch, "E359", {"start": v(-13.8, 4.06) * mm, "end": v(-13.78, 4.1) * mm});
            skLineSegment(sketch, "E360", {"start": v(-13.78, 4.1) * mm, "end": v(-13.75, 4.12) * mm});
            skLineSegment(sketch, "E361", {"start": v(-13.75, 4.12) * mm, "end": v(-13.72, 4.14) * mm});
            skLineSegment(sketch, "E362", {"start": v(-13.72, 4.14) * mm, "end": v(-13.7, 4.17) * mm});
            skLineSegment(sketch, "E363", {"start": v(-13.7, 4.17) * mm, "end": v(-13.66, 4.19) * mm});
            skLineSegment(sketch, "E364", {"start": v(-13.66, 4.19) * mm, "end": v(-13.63, 4.2) * mm});
            skLineSegment(sketch, "E365", {"start": v(12.16, 4.22) * mm, "end": v(12.22, 4.21) * mm});
            skLineSegment(sketch, "E366", {"start": v(12.22, 4.21) * mm, "end": v(12.28, 4.21) * mm});
            skLineSegment(sketch, "E367", {"start": v(12.28, 4.21) * mm, "end": v(12.34, 4.2) * mm});
            skLineSegment(sketch, "E368", {"start": v(12.34, 4.2) * mm, "end": v(12.4, 4.2) * mm});
            skLineSegment(sketch, "E369", {"start": v(12.4, 4.2) * mm, "end": v(12.46, 4.21) * mm});
            skLineSegment(sketch, "E370", {"start": v(12.46, 4.21) * mm, "end": v(12.59, 4.22) * mm});
            skLineSegment(sketch, "E371", {"start": v(12.59, 4.22) * mm, "end": v(12.98, 4.26) * mm});
            skLineSegment(sketch, "E372", {"start": v(12.98, 4.26) * mm, "end": v(13.04, 4.26) * mm});
            skLineSegment(sketch, "E373", {"start": v(13.04, 4.26) * mm, "end": v(13.1, 4.27) * mm});
            skLineSegment(sketch, "E374", {"start": v(13.1, 4.27) * mm, "end": v(13.17, 4.27) * mm});
            skLineSegment(sketch, "E375", {"start": v(13.17, 4.27) * mm, "end": v(13.23, 4.27) * mm});
            skLineSegment(sketch, "E376", {"start": v(13.23, 4.27) * mm, "end": v(13.3, 4.26) * mm});
            skLineSegment(sketch, "E377", {"start": v(13.3, 4.26) * mm, "end": v(13.35, 4.26) * mm});
            skLineSegment(sketch, "E378", {"start": v(13.35, 4.26) * mm, "end": v(13.41, 4.25) * mm});
            skLineSegment(sketch, "E379", {"start": v(13.41, 4.25) * mm, "end": v(13.47, 4.24) * mm});
            skLineSegment(sketch, "E380", {"start": v(13.47, 4.24) * mm, "end": v(13.53, 4.22) * mm});
            skLineSegment(sketch, "E381", {"start": v(13.53, 4.22) * mm, "end": v(13.58, 4.2) * mm});
            skLineSegment(sketch, "E382", {"start": v(13.58, 4.2) * mm, "end": v(13.64, 4.18) * mm});
            skLineSegment(sketch, "E383", {"start": v(13.64, 4.18) * mm, "end": v(13.69, 4.15) * mm});
            skLineSegment(sketch, "E384", {"start": v(13.69, 4.15) * mm, "end": v(13.74, 4.12) * mm});
            skLineSegment(sketch, "E385", {"start": v(13.74, 4.12) * mm, "end": v(13.79, 4.08) * mm});
            skLineSegment(sketch, "E386", {"start": v(13.79, 4.08) * mm, "end": v(13.83, 4.03) * mm});
            skLineSegment(sketch, "E387", {"start": v(13.83, 4.03) * mm, "end": v(13.87, 3.98) * mm});
            skLineSegment(sketch, "E388", {"start": v(13.87, 3.98) * mm, "end": v(13.9, 3.94) * mm});
            skLineSegment(sketch, "E389", {"start": v(13.9, 3.94) * mm, "end": v(13.9, 3.9) * mm});
            skLineSegment(sketch, "E390", {"start": v(13.9, 3.9) * mm, "end": v(13.92, 3.85) * mm});
            skLineSegment(sketch, "E391", {"start": v(13.92, 3.85) * mm, "end": v(13.95, 3.75) * mm});
            skLineSegment(sketch, "E392", {"start": v(13.95, 3.75) * mm, "end": v(13.97, 3.66) * mm});
            skLineSegment(sketch, "E393", {"start": v(13.97, 3.66) * mm, "end": v(13.99, 3.56) * mm});
            skLineSegment(sketch, "E394", {"start": v(13.99, 3.56) * mm, "end": v(14, 3.47) * mm});
            skLineSegment(sketch, "E395", {"start": v(14, 3.47) * mm, "end": v(14, 3.37) * mm});
            skLineSegment(sketch, "E396", {"start": v(14, 3.37) * mm, "end": v(14.01, 3.22) * mm});
            skLineSegment(sketch, "E397", {"start": v(14.01, 3.22) * mm, "end": v(14, 3.03) * mm});
            skLineSegment(sketch, "E398", {"start": v(14, 3.03) * mm, "end": v(13.98, 2.7) * mm});
            skLineSegment(sketch, "E399", {"start": v(13.98, 2.7) * mm, "end": v(13.97, 2.6) * mm});
            skLineSegment(sketch, "E400", {"start": v(13.97, 2.6) * mm, "end": v(13.9, 2.4) * mm});
            skLineSegment(sketch, "E401", {"start": v(13.9, 2.4) * mm, "end": v(13.85, 2.3) * mm});
            skLineSegment(sketch, "E402", {"start": v(13.85, 2.3) * mm, "end": v(13.8, 2.24) * mm});
            skLineSegment(sketch, "E403", {"start": v(13.8, 2.24) * mm, "end": v(13.77, 2.2) * mm});
            skLineSegment(sketch, "E404", {"start": v(13.77, 2.2) * mm, "end": v(13.73, 2.17) * mm});
            skLineSegment(sketch, "E405", {"start": v(13.73, 2.17) * mm, "end": v(13.7, 2.14) * mm});
            skLineSegment(sketch, "E406", {"start": v(13.7, 2.14) * mm, "end": v(13.66, 2.12) * mm});
            skLineSegment(sketch, "E407", {"start": v(13.66, 2.12) * mm, "end": v(13.62, 2.1) * mm});
            skLineSegment(sketch, "E408", {"start": v(13.62, 2.1) * mm, "end": v(12.14, 2.07) * mm});
            skLineSegment(sketch, "E409", {"start": v(12.14, 2.07) * mm, "end": v(12.16, 4.22) * mm});
            skLineSegment(sketch, "E410", {"start": v(-13.64, 0.97) * mm, "end": v(-12.15, 1) * mm});
            skLineSegment(sketch, "E411", {"start": v(-12.15, 1) * mm, "end": v(-12.15, -1.17) * mm});
            skLineSegment(sketch, "E412", {"start": v(-12.15, -1.17) * mm, "end": v(-13.64, -1.14) * mm});
            skLineSegment(sketch, "E413", {"start": v(-13.64, -1.14) * mm, "end": v(-13.83, -0.95) * mm});
            skLineSegment(sketch, "E414", {"start": v(-13.83, -0.95) * mm, "end": v(-13.9, -0.83) * mm});
            skLineSegment(sketch, "E415", {"start": v(-13.9, -0.83) * mm, "end": v(-13.94, -0.75) * mm});
            skLineSegment(sketch, "E416", {"start": v(-13.94, -0.75) * mm, "end": v(-13.97, -0.69) * mm});
            skLineSegment(sketch, "E417", {"start": v(-13.97, -0.69) * mm, "end": v(-13.98, -0.62) * mm});
            skLineSegment(sketch, "E418", {"start": v(-13.98, -0.62) * mm, "end": v(-13.98, -0.6) * mm});
            skLineSegment(sketch, "E419", {"start": v(-13.98, -0.6) * mm, "end": v(-14, -0.49) * mm});
            skLineSegment(sketch, "E420", {"start": v(-14, -0.49) * mm, "end": v(-14.02, -0.25) * mm});
            skLineSegment(sketch, "E421", {"start": v(-14.02, -0.25) * mm, "end": v(-14.03, -0.08) * mm});
            skLineSegment(sketch, "E422", {"start": v(-14.03, -0.08) * mm, "end": v(-14.03, 0.04) * mm});
            skLineSegment(sketch, "E423", {"start": v(-14.03, 0.04) * mm, "end": v(-14.03, 0.1) * mm});
            skLineSegment(sketch, "E424", {"start": v(-14.03, 0.1) * mm, "end": v(-14.03, 0.16) * mm});
            skLineSegment(sketch, "E425", {"start": v(-14.03, 0.16) * mm, "end": v(-14.02, 0.22) * mm});
            skLineSegment(sketch, "E426", {"start": v(-14.02, 0.22) * mm, "end": v(-14.02, 0.28) * mm});
            skLineSegment(sketch, "E427", {"start": v(-14.02, 0.28) * mm, "end": v(-14, 0.34) * mm});
            skLineSegment(sketch, "E428", {"start": v(-14, 0.34) * mm, "end": v(-14, 0.4) * mm});
            skLineSegment(sketch, "E429", {"start": v(-14, 0.4) * mm, "end": v(-13.98, 0.45) * mm});
            skLineSegment(sketch, "E430", {"start": v(-13.98, 0.45) * mm, "end": v(-13.97, 0.5) * mm});
            skLineSegment(sketch, "E431", {"start": v(-13.97, 0.5) * mm, "end": v(-13.95, 0.56) * mm});
            skLineSegment(sketch, "E432", {"start": v(-13.95, 0.56) * mm, "end": v(-13.93, 0.61) * mm});
            skLineSegment(sketch, "E433", {"start": v(-13.93, 0.61) * mm, "end": v(-13.9, 0.66) * mm});
            skLineSegment(sketch, "E434", {"start": v(-13.9, 0.66) * mm, "end": v(-13.88, 0.71) * mm});
            skLineSegment(sketch, "E435", {"start": v(-13.88, 0.71) * mm, "end": v(-13.85, 0.76) * mm});
            skLineSegment(sketch, "E436", {"start": v(-13.85, 0.76) * mm, "end": v(-13.81, 0.8) * mm});
            skLineSegment(sketch, "E437", {"start": v(-13.81, 0.8) * mm, "end": v(-13.78, 0.85) * mm});
            skLineSegment(sketch, "E438", {"start": v(-13.78, 0.85) * mm, "end": v(-13.73, 0.9) * mm});
            skLineSegment(sketch, "E439", {"start": v(-13.73, 0.9) * mm, "end": v(-13.69, 0.94) * mm});
            skLineSegment(sketch, "E440", {"start": v(-13.69, 0.94) * mm, "end": v(-13.64, 0.97) * mm});
            skLineSegment(sketch, "E441", {"start": v(12.14, 1) * mm, "end": v(13.63, 0.97) * mm});
            skLineSegment(sketch, "E442", {"start": v(13.63, 0.97) * mm, "end": v(13.8, 0.8) * mm});
            skLineSegment(sketch, "E443", {"start": v(13.8, 0.8) * mm, "end": v(13.89, 0.69) * mm});
            skLineSegment(sketch, "E444", {"start": v(13.89, 0.69) * mm, "end": v(13.93, 0.6) * mm});
            skLineSegment(sketch, "E445", {"start": v(13.93, 0.6) * mm, "end": v(13.95, 0.54) * mm});
            skLineSegment(sketch, "E446", {"start": v(13.95, 0.54) * mm, "end": v(13.97, 0.48) * mm});
            skLineSegment(sketch, "E447", {"start": v(13.97, 0.48) * mm, "end": v(13.98, 0.43) * mm});
            skLineSegment(sketch, "E448", {"start": v(13.98, 0.43) * mm, "end": v(13.99, 0.32) * mm});
            skLineSegment(sketch, "E449", {"start": v(13.99, 0.32) * mm, "end": v(14, 0.09) * mm});
            skLineSegment(sketch, "E450", {"start": v(14, 0.09) * mm, "end": v(14.02, -0.09) * mm});
            skLineSegment(sketch, "E451", {"start": v(14.02, -0.09) * mm, "end": v(14.02, -0.2) * mm});
            skLineSegment(sketch, "E452", {"start": v(14.02, -0.2) * mm, "end": v(14.02, -0.27) * mm});
            skLineSegment(sketch, "E453", {"start": v(14.02, -0.27) * mm, "end": v(14.02, -0.33) * mm});
            skLineSegment(sketch, "E454", {"start": v(14.02, -0.33) * mm, "end": v(14.02, -0.39) * mm});
            skLineSegment(sketch, "E455", {"start": v(14.02, -0.39) * mm, "end": v(14, -0.45) * mm});
            skLineSegment(sketch, "E456", {"start": v(14, -0.45) * mm, "end": v(14, -0.5) * mm});
            skLineSegment(sketch, "E457", {"start": v(14, -0.5) * mm, "end": v(14, -0.56) * mm});
            skLineSegment(sketch, "E458", {"start": v(14, -0.56) * mm, "end": v(13.98, -0.62) * mm});
            skLineSegment(sketch, "E459", {"start": v(13.98, -0.62) * mm, "end": v(13.96, -0.67) * mm});
            skLineSegment(sketch, "E460", {"start": v(13.96, -0.67) * mm, "end": v(13.94, -0.73) * mm});
            skLineSegment(sketch, "E461", {"start": v(13.94, -0.73) * mm, "end": v(13.92, -0.78) * mm});
            skLineSegment(sketch, "E462", {"start": v(13.92, -0.78) * mm, "end": v(13.9, -0.83) * mm});
            skLineSegment(sketch, "E463", {"start": v(13.9, -0.83) * mm, "end": v(13.87, -0.88) * mm});
            skLineSegment(sketch, "E464", {"start": v(13.87, -0.88) * mm, "end": v(13.84, -0.93) * mm});
            skLineSegment(sketch, "E465", {"start": v(13.84, -0.93) * mm, "end": v(13.8, -0.97) * mm});
            skLineSegment(sketch, "E466", {"start": v(13.8, -0.97) * mm, "end": v(13.77, -1.02) * mm});
            skLineSegment(sketch, "E467", {"start": v(13.77, -1.02) * mm, "end": v(13.73, -1.06) * mm});
            skLineSegment(sketch, "E468", {"start": v(13.73, -1.06) * mm, "end": v(13.68, -1.1) * mm});
            skLineSegment(sketch, "E469", {"start": v(13.68, -1.1) * mm, "end": v(13.63, -1.14) * mm});
            skLineSegment(sketch, "E470", {"start": v(13.63, -1.14) * mm, "end": v(12.14, -1.17) * mm});
            skLineSegment(sketch, "E471", {"start": v(12.14, -1.17) * mm, "end": v(12.14, 1) * mm});
            skLineSegment(sketch, "E472", {"start": v(-13.67, -2.29) * mm, "end": v(-13.52, -2.27) * mm});
            skLineSegment(sketch, "E473", {"start": v(-13.52, -2.27) * mm, "end": v(-13.25, -2.24) * mm});
            skLineSegment(sketch, "E474", {"start": v(-13.25, -2.24) * mm, "end": v(-12.15, -2.23) * mm});
            skLineSegment(sketch, "E475", {"start": v(-12.15, -2.23) * mm, "end": v(-12.17, -4.39) * mm});
            skLineSegment(sketch, "E476", {"start": v(-12.17, -4.39) * mm, "end": v(-13.19, -4.41) * mm});
            skLineSegment(sketch, "E477", {"start": v(-13.19, -4.41) * mm, "end": v(-13.38, -4.4) * mm});
            skLineSegment(sketch, "E478", {"start": v(-13.38, -4.4) * mm, "end": v(-13.52, -4.38) * mm});
            skLineSegment(sketch, "E479", {"start": v(-13.52, -4.38) * mm, "end": v(-13.57, -4.38) * mm});
            skLineSegment(sketch, "E480", {"start": v(-13.57, -4.38) * mm, "end": v(-13.61, -4.36) * mm});
            skLineSegment(sketch, "E481", {"start": v(-13.61, -4.36) * mm, "end": v(-13.65, -4.35) * mm});
            skLineSegment(sketch, "E482", {"start": v(-13.65, -4.35) * mm, "end": v(-13.69, -4.33) * mm});
            skLineSegment(sketch, "E483", {"start": v(-13.69, -4.33) * mm, "end": v(-13.72, -4.3) * mm});
            skLineSegment(sketch, "E484", {"start": v(-13.72, -4.3) * mm, "end": v(-13.75, -4.28) * mm});
            skLineSegment(sketch, "E485", {"start": v(-13.75, -4.28) * mm, "end": v(-13.78, -4.26) * mm});
            skLineSegment(sketch, "E486", {"start": v(-13.78, -4.26) * mm, "end": v(-13.8, -4.23) * mm});
            skLineSegment(sketch, "E487", {"start": v(-13.8, -4.23) * mm, "end": v(-13.83, -4.2) * mm});
            skLineSegment(sketch, "E488", {"start": v(-13.83, -4.2) * mm, "end": v(-13.85, -4.17) * mm});
            skLineSegment(sketch, "E489", {"start": v(-13.85, -4.17) * mm, "end": v(-13.87, -4.13) * mm});
            skLineSegment(sketch, "E490", {"start": v(-13.87, -4.13) * mm, "end": v(-13.9, -4.1) * mm});
            skLineSegment(sketch, "E491", {"start": v(-13.9, -4.1) * mm, "end": v(-13.9, -4.06) * mm});
            skLineSegment(sketch, "E492", {"start": v(-13.9, -4.06) * mm, "end": v(-13.93, -4.02) * mm});
            skLineSegment(sketch, "E493", {"start": v(-13.93, -4.02) * mm, "end": v(-13.94, -3.99) * mm});
            skLineSegment(sketch, "E494", {"start": v(-13.94, -3.99) * mm, "end": v(-13.95, -3.95) * mm});
            skLineSegment(sketch, "E495", {"start": v(-13.95, -3.95) * mm, "end": v(-13.96, -3.9) * mm});
            skLineSegment(sketch, "E496", {"start": v(-13.96, -3.9) * mm, "end": v(-13.98, -3.82) * mm});
            skLineSegment(sketch, "E497", {"start": v(-13.98, -3.82) * mm, "end": v(-14, -3.74) * mm});
            skLineSegment(sketch, "E498", {"start": v(-14, -3.74) * mm, "end": v(-14, -3.62) * mm});
            skLineSegment(sketch, "E499", {"start": v(-14, -3.62) * mm, "end": v(-14.02, -3.5) * mm});
            skLineSegment(sketch, "E500", {"start": v(-14.02, -3.5) * mm, "end": v(-14.02, -3.42) * mm});
            skLineSegment(sketch, "E501", {"start": v(-14.02, -3.42) * mm, "end": v(-14.02, -3.38) * mm});
            skLineSegment(sketch, "E502", {"start": v(-14.02, -3.38) * mm, "end": v(-14.02, -3.27) * mm});
            skLineSegment(sketch, "E503", {"start": v(-14.02, -3.27) * mm, "end": v(-14.01, -3.06) * mm});
            skLineSegment(sketch, "E504", {"start": v(-14.01, -3.06) * mm, "end": v(-14, -2.93) * mm});
            skLineSegment(sketch, "E505", {"start": v(-14, -2.93) * mm, "end": v(-13.99, -2.85) * mm});
            skLineSegment(sketch, "E506", {"start": v(-13.99, -2.85) * mm, "end": v(-13.97, -2.76) * mm});
            skLineSegment(sketch, "E507", {"start": v(-13.97, -2.76) * mm, "end": v(-13.96, -2.72) * mm});
            skLineSegment(sketch, "E508", {"start": v(-13.96, -2.72) * mm, "end": v(-13.95, -2.68) * mm});
            skLineSegment(sketch, "E509", {"start": v(-13.95, -2.68) * mm, "end": v(-13.94, -2.64) * mm});
            skLineSegment(sketch, "E510", {"start": v(-13.94, -2.64) * mm, "end": v(-13.92, -2.6) * mm});
            skLineSegment(sketch, "E511", {"start": v(-13.92, -2.6) * mm, "end": v(-13.9, -2.57) * mm});
            skLineSegment(sketch, "E512", {"start": v(-13.9, -2.57) * mm, "end": v(-13.9, -2.53) * mm});
            skLineSegment(sketch, "E513", {"start": v(-13.9, -2.53) * mm, "end": v(-13.87, -2.5) * mm});
            skLineSegment(sketch, "E514", {"start": v(-13.87, -2.5) * mm, "end": v(-13.85, -2.46) * mm});
            skLineSegment(sketch, "E515", {"start": v(-13.85, -2.46) * mm, "end": v(-13.82, -2.43) * mm});
            skLineSegment(sketch, "E516", {"start": v(-13.82, -2.43) * mm, "end": v(-13.8, -2.4) * mm});
            skLineSegment(sketch, "E517", {"start": v(-13.8, -2.4) * mm, "end": v(-13.77, -2.37) * mm});
            skLineSegment(sketch, "E518", {"start": v(-13.77, -2.37) * mm, "end": v(-13.74, -2.34) * mm});
            skLineSegment(sketch, "E519", {"start": v(-13.74, -2.34) * mm, "end": v(-13.7, -2.31) * mm});
            skLineSegment(sketch, "E520", {"start": v(-13.7, -2.31) * mm, "end": v(-13.67, -2.29) * mm});
            skLineSegment(sketch, "E521", {"start": v(12.14, -2.23) * mm, "end": v(13.8, -2.28) * mm});
            skLineSegment(sketch, "E522", {"start": v(13.8, -2.28) * mm, "end": v(13.84, -2.4) * mm});
            skLineSegment(sketch, "E523", {"start": v(13.84, -2.4) * mm, "end": v(13.87, -2.5) * mm});
            skLineSegment(sketch, "E524", {"start": v(13.87, -2.5) * mm, "end": v(13.9, -2.6) * mm});
            skLineSegment(sketch, "E525", {"start": v(13.9, -2.6) * mm, "end": v(13.94, -2.72) * mm});
            skLineSegment(sketch, "E526", {"start": v(13.94, -2.72) * mm, "end": v(13.96, -2.83) * mm});
            skLineSegment(sketch, "E527", {"start": v(13.96, -2.83) * mm, "end": v(13.98, -2.95) * mm});
            skLineSegment(sketch, "E528", {"start": v(13.98, -2.95) * mm, "end": v(14, -3.06) * mm});
            skLineSegment(sketch, "E529", {"start": v(14, -3.06) * mm, "end": v(14.01, -3.18) * mm});
            skLineSegment(sketch, "E530", {"start": v(14.01, -3.18) * mm, "end": v(14.02, -3.3) * mm});
            skLineSegment(sketch, "E531", {"start": v(14.02, -3.3) * mm, "end": v(14.02, -3.35) * mm});
            skLineSegment(sketch, "E532", {"start": v(14.02, -3.35) * mm, "end": v(14.02, -3.4) * mm});
            skLineSegment(sketch, "E533", {"start": v(14.02, -3.4) * mm, "end": v(14.01, -3.47) * mm});
            skLineSegment(sketch, "E534", {"start": v(14.01, -3.47) * mm, "end": v(14.01, -3.52) * mm});
            skLineSegment(sketch, "E535", {"start": v(14.01, -3.52) * mm, "end": v(14, -3.58) * mm});
            skLineSegment(sketch, "E536", {"start": v(14, -3.58) * mm, "end": v(14, -3.64) * mm});
            skLineSegment(sketch, "E537", {"start": v(14, -3.64) * mm, "end": v(14, -3.7) * mm});
            skLineSegment(sketch, "E538", {"start": v(14, -3.7) * mm, "end": v(13.98, -3.75) * mm});
            skLineSegment(sketch, "E539", {"start": v(13.98, -3.75) * mm, "end": v(13.97, -3.81) * mm});
            skLineSegment(sketch, "E540", {"start": v(13.97, -3.81) * mm, "end": v(13.96, -3.87) * mm});
            skLineSegment(sketch, "E541", {"start": v(13.96, -3.87) * mm, "end": v(13.95, -3.92) * mm});
            skLineSegment(sketch, "E542", {"start": v(13.95, -3.92) * mm, "end": v(13.93, -4) * mm});
            skLineSegment(sketch, "E543", {"start": v(13.93, -4) * mm, "end": v(13.9, -4.09) * mm});
            skLineSegment(sketch, "E544", {"start": v(13.9, -4.09) * mm, "end": v(13.85, -4.16) * mm});
            skLineSegment(sketch, "E545", {"start": v(13.85, -4.16) * mm, "end": v(13.81, -4.22) * mm});
            skLineSegment(sketch, "E546", {"start": v(13.81, -4.22) * mm, "end": v(13.77, -4.26) * mm});
            skLineSegment(sketch, "E547", {"start": v(13.77, -4.26) * mm, "end": v(13.74, -4.3) * mm});
            skLineSegment(sketch, "E548", {"start": v(13.74, -4.3) * mm, "end": v(13.7, -4.32) * mm});
            skLineSegment(sketch, "E549", {"start": v(13.7, -4.32) * mm, "end": v(13.66, -4.34) * mm});
            skLineSegment(sketch, "E550", {"start": v(13.66, -4.34) * mm, "end": v(13.62, -4.35) * mm});
            skLineSegment(sketch, "E551", {"start": v(13.62, -4.35) * mm, "end": v(13.58, -4.37) * mm});
            skLineSegment(sketch, "E552", {"start": v(13.58, -4.37) * mm, "end": v(13.56, -4.37) * mm});
            skLineSegment(sketch, "E553", {"start": v(13.56, -4.37) * mm, "end": v(12.16, -4.4) * mm});
            skLineSegment(sketch, "E554", {"start": v(12.16, -4.4) * mm, "end": v(12.14, -2.23) * mm});
            skLineSegment(sketch, "E555", {"start": v(-13.8, -5.52) * mm, "end": v(-12.15, -5.47) * mm});
            skLineSegment(sketch, "E556", {"start": v(-12.15, -5.47) * mm, "end": v(-12.17, -7.63) * mm});
            skLineSegment(sketch, "E557", {"start": v(-12.17, -7.63) * mm, "end": v(-12.23, -7.62) * mm});
            skLineSegment(sketch, "E558", {"start": v(-12.23, -7.62) * mm, "end": v(-12.29, -7.62) * mm});
            skLineSegment(sketch, "E559", {"start": v(-12.29, -7.62) * mm, "end": v(-12.35, -7.61) * mm});
            skLineSegment(sketch, "E560", {"start": v(-12.35, -7.61) * mm, "end": v(-12.4, -7.61) * mm});
            skLineSegment(sketch, "E561", {"start": v(-12.4, -7.61) * mm, "end": v(-12.47, -7.62) * mm});
            skLineSegment(sketch, "E562", {"start": v(-12.47, -7.62) * mm, "end": v(-12.6, -7.63) * mm});
            skLineSegment(sketch, "E563", {"start": v(-12.6, -7.63) * mm, "end": v(-12.98, -7.66) * mm});
            skLineSegment(sketch, "E564", {"start": v(-12.98, -7.66) * mm, "end": v(-13.05, -7.67) * mm});
            skLineSegment(sketch, "E565", {"start": v(-13.05, -7.67) * mm, "end": v(-13.1, -7.67) * mm});
            skLineSegment(sketch, "E566", {"start": v(-13.1, -7.67) * mm, "end": v(-13.17, -7.67) * mm});
            skLineSegment(sketch, "E567", {"start": v(-13.17, -7.67) * mm, "end": v(-13.24, -7.67) * mm});
            skLineSegment(sketch, "E568", {"start": v(-13.24, -7.67) * mm, "end": v(-13.3, -7.67) * mm});
            skLineSegment(sketch, "E569", {"start": v(-13.3, -7.67) * mm, "end": v(-13.36, -7.66) * mm});
            skLineSegment(sketch, "E570", {"start": v(-13.36, -7.66) * mm, "end": v(-13.42, -7.65) * mm});
            skLineSegment(sketch, "E571", {"start": v(-13.42, -7.65) * mm, "end": v(-13.48, -7.64) * mm});
            skLineSegment(sketch, "E572", {"start": v(-13.48, -7.64) * mm, "end": v(-13.53, -7.63) * mm});
            skLineSegment(sketch, "E573", {"start": v(-13.53, -7.63) * mm, "end": v(-13.59, -7.6) * mm});
            skLineSegment(sketch, "E574", {"start": v(-13.59, -7.6) * mm, "end": v(-13.64, -7.58) * mm});
            skLineSegment(sketch, "E575", {"start": v(-13.64, -7.58) * mm, "end": v(-13.7, -7.55) * mm});
            skLineSegment(sketch, "E576", {"start": v(-13.7, -7.55) * mm, "end": v(-13.74, -7.52) * mm});
            skLineSegment(sketch, "E577", {"start": v(-13.74, -7.52) * mm, "end": v(-13.8, -7.48) * mm});
            skLineSegment(sketch, "E578", {"start": v(-13.8, -7.48) * mm, "end": v(-13.84, -7.44) * mm});
            skLineSegment(sketch, "E579", {"start": v(-13.84, -7.44) * mm, "end": v(-13.88, -7.39) * mm});
            skLineSegment(sketch, "E580", {"start": v(-13.88, -7.39) * mm, "end": v(-13.9, -7.33) * mm});
            skLineSegment(sketch, "E581", {"start": v(-13.9, -7.33) * mm, "end": v(-13.92, -7.26) * mm});
            skLineSegment(sketch, "E582", {"start": v(-13.92, -7.26) * mm, "end": v(-13.94, -7.2) * mm});
            skLineSegment(sketch, "E583", {"start": v(-13.94, -7.2) * mm, "end": v(-13.96, -7.14) * mm});
            skLineSegment(sketch, "E584", {"start": v(-13.96, -7.14) * mm, "end": v(-13.97, -7.07) * mm});
            skLineSegment(sketch, "E585", {"start": v(-13.97, -7.07) * mm, "end": v(-13.99, -7) * mm});
            skLineSegment(sketch, "E586", {"start": v(-13.99, -7) * mm, "end": v(-14, -6.94) * mm});
            skLineSegment(sketch, "E587", {"start": v(-14, -6.94) * mm, "end": v(-14, -6.88) * mm});
            skLineSegment(sketch, "E588", {"start": v(-14, -6.88) * mm, "end": v(-14.01, -6.81) * mm});
            skLineSegment(sketch, "E589", {"start": v(-14.01, -6.81) * mm, "end": v(-14.02, -6.75) * mm});
            skLineSegment(sketch, "E590", {"start": v(-14.02, -6.75) * mm, "end": v(-14.02, -6.68) * mm});
            skLineSegment(sketch, "E591", {"start": v(-14.02, -6.68) * mm, "end": v(-14.02, -6.62) * mm});
            skLineSegment(sketch, "E592", {"start": v(-14.02, -6.62) * mm, "end": v(-14.02, -6.55) * mm});
            skLineSegment(sketch, "E593", {"start": v(-14.02, -6.55) * mm, "end": v(-14.02, -6.48) * mm});
            skLineSegment(sketch, "E594", {"start": v(-14.02, -6.48) * mm, "end": v(-14.02, -6.42) * mm});
            skLineSegment(sketch, "E595", {"start": v(-14.02, -6.42) * mm, "end": v(-14.01, -6.35) * mm});
            skLineSegment(sketch, "E596", {"start": v(-14.01, -6.35) * mm, "end": v(-14, -6.29) * mm});
            skLineSegment(sketch, "E597", {"start": v(-14, -6.29) * mm, "end": v(-14, -6.22) * mm});
            skLineSegment(sketch, "E598", {"start": v(-14, -6.22) * mm, "end": v(-13.99, -6.15) * mm});
            skLineSegment(sketch, "E599", {"start": v(-13.99, -6.15) * mm, "end": v(-13.97, -6.09) * mm});
            skLineSegment(sketch, "E600", {"start": v(-13.97, -6.09) * mm, "end": v(-13.96, -6.03) * mm});
            skLineSegment(sketch, "E601", {"start": v(-13.96, -6.03) * mm, "end": v(-13.95, -5.96) * mm});
            skLineSegment(sketch, "E602", {"start": v(-13.95, -5.96) * mm, "end": v(-13.93, -5.9) * mm});
            skLineSegment(sketch, "E603", {"start": v(-13.93, -5.9) * mm, "end": v(-13.91, -5.83) * mm});
            skLineSegment(sketch, "E604", {"start": v(-13.91, -5.83) * mm, "end": v(-13.9, -5.77) * mm});
            skLineSegment(sketch, "E605", {"start": v(-13.9, -5.77) * mm, "end": v(-13.87, -5.7) * mm});
            skLineSegment(sketch, "E606", {"start": v(-13.87, -5.7) * mm, "end": v(-13.85, -5.65) * mm});
            skLineSegment(sketch, "E607", {"start": v(-13.85, -5.65) * mm, "end": v(-13.82, -5.58) * mm});
            skLineSegment(sketch, "E608", {"start": v(-13.82, -5.58) * mm, "end": v(-13.8, -5.52) * mm});
            skLineSegment(sketch, "E609", {"start": v(12.14, -5.47) * mm, "end": v(13.8, -5.52) * mm});
            skLineSegment(sketch, "E610", {"start": v(13.8, -5.52) * mm, "end": v(13.82, -5.59) * mm});
            skLineSegment(sketch, "E611", {"start": v(13.82, -5.59) * mm, "end": v(13.84, -5.66) * mm});
            skLineSegment(sketch, "E612", {"start": v(13.84, -5.66) * mm, "end": v(13.87, -5.73) * mm});
            skLineSegment(sketch, "E613", {"start": v(13.87, -5.73) * mm, "end": v(13.89, -5.8) * mm});
            skLineSegment(sketch, "E614", {"start": v(13.89, -5.8) * mm, "end": v(13.91, -5.87) * mm});
            skLineSegment(sketch, "E615", {"start": v(13.91, -5.87) * mm, "end": v(13.93, -5.94) * mm});
            skLineSegment(sketch, "E616", {"start": v(13.93, -5.94) * mm, "end": v(13.95, -6.02) * mm});
            skLineSegment(sketch, "E617", {"start": v(13.95, -6.02) * mm, "end": v(13.97, -6.1) * mm});
            skLineSegment(sketch, "E618", {"start": v(13.97, -6.1) * mm, "end": v(13.98, -6.17) * mm});
            skLineSegment(sketch, "E619", {"start": v(13.98, -6.17) * mm, "end": v(14, -6.24) * mm});
            skLineSegment(sketch, "E620", {"start": v(14, -6.24) * mm, "end": v(14, -6.32) * mm});
            skLineSegment(sketch, "E621", {"start": v(14, -6.32) * mm, "end": v(14.02, -6.4) * mm});
            skLineSegment(sketch, "E622", {"start": v(14.02, -6.4) * mm, "end": v(14.02, -6.47) * mm});
            skLineSegment(sketch, "E623", {"start": v(14.02, -6.47) * mm, "end": v(14.03, -6.55) * mm});
            skLineSegment(sketch, "E624", {"start": v(14.03, -6.55) * mm, "end": v(14.03, -6.62) * mm});
            skLineSegment(sketch, "E625", {"start": v(14.03, -6.62) * mm, "end": v(14.03, -6.7) * mm});
            skLineSegment(sketch, "E626", {"start": v(14.03, -6.7) * mm, "end": v(14.02, -6.77) * mm});
            skLineSegment(sketch, "E627", {"start": v(14.02, -6.77) * mm, "end": v(14.02, -6.85) * mm});
            skLineSegment(sketch, "E628", {"start": v(14.02, -6.85) * mm, "end": v(14, -6.92) * mm});
            skLineSegment(sketch, "E629", {"start": v(14, -6.92) * mm, "end": v(14, -7) * mm});
            skLineSegment(sketch, "E630", {"start": v(14, -7) * mm, "end": v(13.98, -7.06) * mm});
            skLineSegment(sketch, "E631", {"start": v(13.98, -7.06) * mm, "end": v(13.96, -7.13) * mm});
            skLineSegment(sketch, "E632", {"start": v(13.96, -7.13) * mm, "end": v(13.93, -7.2) * mm});
            skLineSegment(sketch, "E633", {"start": v(13.93, -7.2) * mm, "end": v(13.9, -7.27) * mm});
            skLineSegment(sketch, "E634", {"start": v(13.9, -7.27) * mm, "end": v(13.87, -7.33) * mm});
            skLineSegment(sketch, "E635", {"start": v(13.87, -7.33) * mm, "end": v(13.83, -7.4) * mm});
            skLineSegment(sketch, "E636", {"start": v(13.83, -7.4) * mm, "end": v(13.8, -7.45) * mm});
            skLineSegment(sketch, "E637", {"start": v(13.8, -7.45) * mm, "end": v(13.75, -7.51) * mm});
            skLineSegment(sketch, "E638", {"start": v(13.75, -7.51) * mm, "end": v(13.7, -7.57) * mm});
            skLineSegment(sketch, "E639", {"start": v(13.7, -7.57) * mm, "end": v(13.65, -7.58) * mm});
            skLineSegment(sketch, "E640", {"start": v(13.65, -7.58) * mm, "end": v(13.6, -7.6) * mm});
            skLineSegment(sketch, "E641", {"start": v(13.6, -7.6) * mm, "end": v(13.54, -7.6) * mm});
            skLineSegment(sketch, "E642", {"start": v(13.54, -7.6) * mm, "end": v(13.5, -7.62) * mm});
            skLineSegment(sketch, "E643", {"start": v(13.5, -7.62) * mm, "end": v(13.44, -7.63) * mm});
            skLineSegment(sketch, "E644", {"start": v(13.44, -7.63) * mm, "end": v(13.34, -7.64) * mm});
            skLineSegment(sketch, "E645", {"start": v(13.34, -7.64) * mm, "end": v(13.23, -7.65) * mm});
            skLineSegment(sketch, "E646", {"start": v(13.23, -7.65) * mm, "end": v(13.07, -7.65) * mm});
            skLineSegment(sketch, "E647", {"start": v(13.07, -7.65) * mm, "end": v(12.32, -7.63) * mm});
            skLineSegment(sketch, "E648", {"start": v(12.32, -7.63) * mm, "end": v(12.16, -7.63) * mm});
            skLineSegment(sketch, "E649", {"start": v(12.16, -7.63) * mm, "end": v(12.14, -5.47) * mm});
            skLineSegment(sketch, "E650", {"start": v(-5.9, -10.04) * mm, "end": v(-3.75, -10.04) * mm});
            skLineSegment(sketch, "E651", {"start": v(-3.75, -10.04) * mm, "end": v(-3.75, -11.23) * mm});
            skLineSegment(sketch, "E652", {"start": v(-3.75, -11.23) * mm, "end": v(-3.77, -11.42) * mm});
            skLineSegment(sketch, "E653", {"start": v(-3.77, -11.42) * mm, "end": v(-3.77, -11.44) * mm});
            skLineSegment(sketch, "E654", {"start": v(-3.77, -11.44) * mm, "end": v(-3.78, -11.47) * mm});
            skLineSegment(sketch, "E655", {"start": v(-3.78, -11.47) * mm, "end": v(-3.78, -11.5) * mm});
            skLineSegment(sketch, "E656", {"start": v(-3.78, -11.5) * mm, "end": v(-3.8, -11.51) * mm});
            skLineSegment(sketch, "E657", {"start": v(-3.8, -11.51) * mm, "end": v(-3.8, -11.54) * mm});
            skLineSegment(sketch, "E658", {"start": v(-3.8, -11.54) * mm, "end": v(-3.82, -11.56) * mm});
            skLineSegment(sketch, "E659", {"start": v(-3.82, -11.56) * mm, "end": v(-3.83, -11.58) * mm});
            skLineSegment(sketch, "E660", {"start": v(-3.83, -11.58) * mm, "end": v(-3.84, -11.6) * mm});
            skLineSegment(sketch, "E661", {"start": v(-3.84, -11.6) * mm, "end": v(-3.86, -11.61) * mm});
            skLineSegment(sketch, "E662", {"start": v(-3.86, -11.61) * mm, "end": v(-3.9, -11.65) * mm});
            skLineSegment(sketch, "E663", {"start": v(-3.9, -11.65) * mm, "end": v(-3.93, -11.68) * mm});
            skLineSegment(sketch, "E664", {"start": v(-3.93, -11.68) * mm, "end": v(-4, -11.72) * mm});
            skLineSegment(sketch, "E665", {"start": v(-4, -11.72) * mm, "end": v(-4.1, -11.78) * mm});
            skLineSegment(sketch, "E666", {"start": v(-4.1, -11.78) * mm, "end": v(-4.3, -11.85) * mm});
            skLineSegment(sketch, "E667", {"start": v(-4.3, -11.85) * mm, "end": v(-4.4, -11.87) * mm});
            skLineSegment(sketch, "E668", {"start": v(-4.4, -11.87) * mm, "end": v(-4.46, -11.88) * mm});
            skLineSegment(sketch, "E669", {"start": v(-4.46, -11.88) * mm, "end": v(-4.52, -11.89) * mm});
            skLineSegment(sketch, "E670", {"start": v(-4.52, -11.89) * mm, "end": v(-4.58, -11.9) * mm});
            skLineSegment(sketch, "E671", {"start": v(-4.58, -11.9) * mm, "end": v(-4.64, -11.9) * mm});
            skLineSegment(sketch, "E672", {"start": v(-4.64, -11.9) * mm, "end": v(-4.7, -11.9) * mm});
            skLineSegment(sketch, "E673", {"start": v(-4.7, -11.9) * mm, "end": v(-4.76, -11.9) * mm});
            skLineSegment(sketch, "E674", {"start": v(-4.76, -11.9) * mm, "end": v(-4.82, -11.9) * mm});
            skLineSegment(sketch, "E675", {"start": v(-4.82, -11.9) * mm, "end": v(-4.88, -11.9) * mm});
            skLineSegment(sketch, "E676", {"start": v(-4.88, -11.9) * mm, "end": v(-4.94, -11.9) * mm});
            skLineSegment(sketch, "E677", {"start": v(-4.94, -11.9) * mm, "end": v(-5, -11.9) * mm});
            skLineSegment(sketch, "E678", {"start": v(-5, -11.9) * mm, "end": v(-5.05, -11.9) * mm});
            skLineSegment(sketch, "E679", {"start": v(-5.05, -11.9) * mm, "end": v(-5.11, -11.9) * mm});
            skLineSegment(sketch, "E680", {"start": v(-5.11, -11.9) * mm, "end": v(-5.17, -11.89) * mm});
            skLineSegment(sketch, "E681", {"start": v(-5.17, -11.89) * mm, "end": v(-5.23, -11.88) * mm});
            skLineSegment(sketch, "E682", {"start": v(-5.23, -11.88) * mm, "end": v(-5.29, -11.86) * mm});
            skLineSegment(sketch, "E683", {"start": v(-5.29, -11.86) * mm, "end": v(-5.34, -11.85) * mm});
            skLineSegment(sketch, "E684", {"start": v(-5.34, -11.85) * mm, "end": v(-5.4, -11.84) * mm});
            skLineSegment(sketch, "E685", {"start": v(-5.4, -11.84) * mm, "end": v(-5.46, -11.82) * mm});
            skLineSegment(sketch, "E686", {"start": v(-5.46, -11.82) * mm, "end": v(-5.51, -11.8) * mm});
            skLineSegment(sketch, "E687", {"start": v(-5.51, -11.8) * mm, "end": v(-5.57, -11.78) * mm});
            skLineSegment(sketch, "E688", {"start": v(-5.57, -11.78) * mm, "end": v(-5.62, -11.75) * mm});
            skLineSegment(sketch, "E689", {"start": v(-5.62, -11.75) * mm, "end": v(-5.67, -11.73) * mm});
            skLineSegment(sketch, "E690", {"start": v(-5.67, -11.73) * mm, "end": v(-5.72, -11.7) * mm});
            skLineSegment(sketch, "E691", {"start": v(-5.72, -11.7) * mm, "end": v(-5.78, -11.67) * mm});
            skLineSegment(sketch, "E692", {"start": v(-5.78, -11.67) * mm, "end": v(-5.83, -11.64) * mm});
            skLineSegment(sketch, "E693", {"start": v(-5.83, -11.64) * mm, "end": v(-5.88, -11.6) * mm});
            skLineSegment(sketch, "E694", {"start": v(-5.88, -11.6) * mm, "end": v(-5.92, -11.57) * mm});
            skLineSegment(sketch, "E695", {"start": v(-5.92, -11.57) * mm, "end": v(-5.9, -10.04) * mm});
            skLineSegment(sketch, "E696", {"start": v(-2.74, -10.04) * mm, "end": v(-0.56, -10.04) * mm});
            skLineSegment(sketch, "E697", {"start": v(-0.56, -10.04) * mm, "end": v(-0.53, -11.25) * mm});
            skLineSegment(sketch, "E698", {"start": v(-0.53, -11.25) * mm, "end": v(-0.54, -11.34) * mm});
            skLineSegment(sketch, "E699", {"start": v(-0.54, -11.34) * mm, "end": v(-0.56, -11.42) * mm});
            skLineSegment(sketch, "E700", {"start": v(-0.56, -11.42) * mm, "end": v(-0.6, -11.49) * mm});
            skLineSegment(sketch, "E701", {"start": v(-0.6, -11.49) * mm, "end": v(-0.63, -11.56) * mm});
            skLineSegment(sketch, "E702", {"start": v(-0.63, -11.56) * mm, "end": v(-0.68, -11.62) * mm});
            skLineSegment(sketch, "E703", {"start": v(-0.68, -11.62) * mm, "end": v(-0.7, -11.67) * mm});
            skLineSegment(sketch, "E704", {"start": v(-0.7, -11.67) * mm, "end": v(-0.75, -11.7) * mm});
            skLineSegment(sketch, "E705", {"start": v(-0.75, -11.7) * mm, "end": v(-0.79, -11.74) * mm});
            skLineSegment(sketch, "E706", {"start": v(-0.79, -11.74) * mm, "end": v(-0.83, -11.77) * mm});
            skLineSegment(sketch, "E707", {"start": v(-0.83, -11.77) * mm, "end": v(-0.87, -11.8) * mm});
            skLineSegment(sketch, "E708", {"start": v(-0.87, -11.8) * mm, "end": v(-0.9, -11.8) * mm});
            skLineSegment(sketch, "E709", {"start": v(-0.9, -11.8) * mm, "end": v(-0.92, -11.81) * mm});
            skLineSegment(sketch, "E710", {"start": v(-0.92, -11.81) * mm, "end": v(-0.95, -11.82) * mm});
            skLineSegment(sketch, "E711", {"start": v(-0.95, -11.82) * mm, "end": v(-0.97, -11.83) * mm});
            skLineSegment(sketch, "E712", {"start": v(-0.97, -11.83) * mm, "end": v(-1, -11.84) * mm});
            skLineSegment(sketch, "E713", {"start": v(-1, -11.84) * mm, "end": v(-1.02, -11.84) * mm});
            skLineSegment(sketch, "E714", {"start": v(-1.02, -11.84) * mm, "end": v(-1.05, -11.84) * mm});
            skLineSegment(sketch, "E715", {"start": v(-1.05, -11.84) * mm, "end": v(-1.1, -11.85) * mm});
            skLineSegment(sketch, "E716", {"start": v(-1.1, -11.85) * mm, "end": v(-1.22, -11.88) * mm});
            skLineSegment(sketch, "E717", {"start": v(-1.22, -11.88) * mm, "end": v(-1.34, -11.9) * mm});
            skLineSegment(sketch, "E718", {"start": v(-1.34, -11.9) * mm, "end": v(-1.47, -11.9) * mm});
            skLineSegment(sketch, "E719", {"start": v(-1.47, -11.9) * mm, "end": v(-1.53, -11.91) * mm});
            skLineSegment(sketch, "E720", {"start": v(-1.53, -11.91) * mm, "end": v(-1.59, -11.91) * mm});
            skLineSegment(sketch, "E721", {"start": v(-1.59, -11.91) * mm, "end": v(-1.65, -11.92) * mm});
            skLineSegment(sketch, "E722", {"start": v(-1.65, -11.92) * mm, "end": v(-1.71, -11.92) * mm});
            skLineSegment(sketch, "E723", {"start": v(-1.71, -11.92) * mm, "end": v(-1.78, -11.91) * mm});
            skLineSegment(sketch, "E724", {"start": v(-1.78, -11.91) * mm, "end": v(-1.84, -11.9) * mm});
            skLineSegment(sketch, "E725", {"start": v(-1.84, -11.9) * mm, "end": v(-1.9, -11.9) * mm});
            skLineSegment(sketch, "E726", {"start": v(-1.9, -11.9) * mm, "end": v(-1.96, -11.9) * mm});
            skLineSegment(sketch, "E727", {"start": v(-1.96, -11.9) * mm, "end": v(-2.02, -11.89) * mm});
            skLineSegment(sketch, "E728", {"start": v(-2.02, -11.89) * mm, "end": v(-2.08, -11.87) * mm});
            skLineSegment(sketch, "E729", {"start": v(-2.08, -11.87) * mm, "end": v(-2.14, -11.86) * mm});
            skLineSegment(sketch, "E730", {"start": v(-2.14, -11.86) * mm, "end": v(-2.2, -11.84) * mm});
            skLineSegment(sketch, "E731", {"start": v(-2.2, -11.84) * mm, "end": v(-2.25, -11.82) * mm});
            skLineSegment(sketch, "E732", {"start": v(-2.25, -11.82) * mm, "end": v(-2.3, -11.8) * mm});
            skLineSegment(sketch, "E733", {"start": v(-2.3, -11.8) * mm, "end": v(-2.36, -11.77) * mm});
            skLineSegment(sketch, "E734", {"start": v(-2.36, -11.77) * mm, "end": v(-2.41, -11.74) * mm});
            skLineSegment(sketch, "E735", {"start": v(-2.41, -11.74) * mm, "end": v(-2.46, -11.7) * mm});
            skLineSegment(sketch, "E736", {"start": v(-2.46, -11.7) * mm, "end": v(-2.5, -11.67) * mm});
            skLineSegment(sketch, "E737", {"start": v(-2.5, -11.67) * mm, "end": v(-2.55, -11.63) * mm});
            skLineSegment(sketch, "E738", {"start": v(-2.55, -11.63) * mm, "end": v(-2.6, -11.58) * mm});
            skLineSegment(sketch, "E739", {"start": v(-2.6, -11.58) * mm, "end": v(-2.64, -11.54) * mm});
            skLineSegment(sketch, "E740", {"start": v(-2.64, -11.54) * mm, "end": v(-2.68, -11.49) * mm});
            skLineSegment(sketch, "E741", {"start": v(-2.68, -11.49) * mm, "end": v(-2.7, -11.39) * mm});
            skLineSegment(sketch, "E742", {"start": v(-2.7, -11.39) * mm, "end": v(-2.71, -11.24) * mm});
            skLineSegment(sketch, "E743", {"start": v(-2.71, -11.24) * mm, "end": v(-2.73, -11) * mm});
            skLineSegment(sketch, "E744", {"start": v(-2.73, -11) * mm, "end": v(-2.74, -10.04) * mm});
            skLineSegment(sketch, "E745", {"start": v(0.56, -10.04) * mm, "end": v(2.73, -10.04) * mm});
            skLineSegment(sketch, "E746", {"start": v(2.73, -10.04) * mm, "end": v(2.74, -11.03) * mm});
            skLineSegment(sketch, "E747", {"start": v(2.74, -11.03) * mm, "end": v(2.72, -11.26) * mm});
            skLineSegment(sketch, "E748", {"start": v(2.72, -11.26) * mm, "end": v(2.7, -11.4) * mm});
            skLineSegment(sketch, "E749", {"start": v(2.7, -11.4) * mm, "end": v(2.68, -11.45) * mm});
            skLineSegment(sketch, "E750", {"start": v(2.68, -11.45) * mm, "end": v(2.66, -11.5) * mm});
            skLineSegment(sketch, "E751", {"start": v(2.66, -11.5) * mm, "end": v(2.63, -11.54) * mm});
            skLineSegment(sketch, "E752", {"start": v(2.63, -11.54) * mm, "end": v(2.6, -11.58) * mm});
            skLineSegment(sketch, "E753", {"start": v(2.6, -11.58) * mm, "end": v(2.57, -11.62) * mm});
            skLineSegment(sketch, "E754", {"start": v(2.57, -11.62) * mm, "end": v(2.54, -11.65) * mm});
            skLineSegment(sketch, "E755", {"start": v(2.54, -11.65) * mm, "end": v(2.5, -11.68) * mm});
            skLineSegment(sketch, "E756", {"start": v(2.5, -11.68) * mm, "end": v(2.46, -11.7) * mm});
            skLineSegment(sketch, "E757", {"start": v(2.46, -11.7) * mm, "end": v(2.42, -11.74) * mm});
            skLineSegment(sketch, "E758", {"start": v(2.42, -11.74) * mm, "end": v(2.38, -11.76) * mm});
            skLineSegment(sketch, "E759", {"start": v(2.38, -11.76) * mm, "end": v(2.34, -11.78) * mm});
            skLineSegment(sketch, "E760", {"start": v(2.34, -11.78) * mm, "end": v(2.3, -11.8) * mm});
            skLineSegment(sketch, "E761", {"start": v(2.3, -11.8) * mm, "end": v(2.25, -11.82) * mm});
            skLineSegment(sketch, "E762", {"start": v(2.25, -11.82) * mm, "end": v(2.2, -11.84) * mm});
            skLineSegment(sketch, "E763", {"start": v(2.2, -11.84) * mm, "end": v(2.15, -11.85) * mm});
            skLineSegment(sketch, "E764", {"start": v(2.15, -11.85) * mm, "end": v(2.1, -11.86) * mm});
            skLineSegment(sketch, "E765", {"start": v(2.1, -11.86) * mm, "end": v(2.06, -11.87) * mm});
            skLineSegment(sketch, "E766", {"start": v(2.06, -11.87) * mm, "end": v(2, -11.88) * mm});
            skLineSegment(sketch, "E767", {"start": v(2, -11.88) * mm, "end": v(1.96, -11.89) * mm});
            skLineSegment(sketch, "E768", {"start": v(1.96, -11.89) * mm, "end": v(1.86, -11.9) * mm});
            skLineSegment(sketch, "E769", {"start": v(1.86, -11.9) * mm, "end": v(1.76, -11.9) * mm});
            skLineSegment(sketch, "E770", {"start": v(1.76, -11.9) * mm, "end": v(1.66, -11.9) * mm});
            skLineSegment(sketch, "E771", {"start": v(1.66, -11.9) * mm, "end": v(1.56, -11.9) * mm});
            skLineSegment(sketch, "E772", {"start": v(1.56, -11.9) * mm, "end": v(1.47, -11.9) * mm});
            skLineSegment(sketch, "E773", {"start": v(1.47, -11.9) * mm, "end": v(1.4, -11.9) * mm});
            skLineSegment(sketch, "E774", {"start": v(1.4, -11.9) * mm, "end": v(1.32, -11.9) * mm});
            skLineSegment(sketch, "E775", {"start": v(1.32, -11.9) * mm, "end": v(1.24, -11.89) * mm});
            skLineSegment(sketch, "E776", {"start": v(1.24, -11.89) * mm, "end": v(1.17, -11.88) * mm});
            skLineSegment(sketch, "E777", {"start": v(1.17, -11.88) * mm, "end": v(1.1, -11.86) * mm});
            skLineSegment(sketch, "E778", {"start": v(1.1, -11.86) * mm, "end": v(1.06, -11.85) * mm});
            skLineSegment(sketch, "E779", {"start": v(1.06, -11.85) * mm, "end": v(1.02, -11.84) * mm});
            skLineSegment(sketch, "E780", {"start": v(1.02, -11.84) * mm, "end": v(0.98, -11.83) * mm});
            skLineSegment(sketch, "E781", {"start": v(0.98, -11.83) * mm, "end": v(0.95, -11.81) * mm});
            skLineSegment(sketch, "E782", {"start": v(0.95, -11.81) * mm, "end": v(0.91, -11.8) * mm});
            skLineSegment(sketch, "E783", {"start": v(0.91, -11.8) * mm, "end": v(0.88, -11.78) * mm});
            skLineSegment(sketch, "E784", {"start": v(0.88, -11.78) * mm, "end": v(0.85, -11.76) * mm});
            skLineSegment(sketch, "E785", {"start": v(0.85, -11.76) * mm, "end": v(0.81, -11.74) * mm});
            skLineSegment(sketch, "E786", {"start": v(0.81, -11.74) * mm, "end": v(0.78, -11.72) * mm});
            skLineSegment(sketch, "E787", {"start": v(0.78, -11.72) * mm, "end": v(0.75, -11.7) * mm});
            skLineSegment(sketch, "E788", {"start": v(0.75, -11.7) * mm, "end": v(0.72, -11.68) * mm});
            skLineSegment(sketch, "E789", {"start": v(0.72, -11.68) * mm, "end": v(0.7, -11.65) * mm});
            skLineSegment(sketch, "E790", {"start": v(0.7, -11.65) * mm, "end": v(0.67, -11.63) * mm});
            skLineSegment(sketch, "E791", {"start": v(0.67, -11.63) * mm, "end": v(0.65, -11.6) * mm});
            skLineSegment(sketch, "E792", {"start": v(0.65, -11.6) * mm, "end": v(0.63, -11.57) * mm});
            skLineSegment(sketch, "E793", {"start": v(0.63, -11.57) * mm, "end": v(0.6, -11.54) * mm});
            skLineSegment(sketch, "E794", {"start": v(0.6, -11.54) * mm, "end": v(0.59, -11.5) * mm});
            skLineSegment(sketch, "E795", {"start": v(0.59, -11.5) * mm, "end": v(0.57, -11.47) * mm});
            skLineSegment(sketch, "E796", {"start": v(0.57, -11.47) * mm, "end": v(0.55, -11.43) * mm});
            skLineSegment(sketch, "E797", {"start": v(0.55, -11.43) * mm, "end": v(0.53, -11.29) * mm});
            skLineSegment(sketch, "E798", {"start": v(0.53, -11.29) * mm, "end": v(0.52, -11.1) * mm});
            skLineSegment(sketch, "E799", {"start": v(0.52, -11.1) * mm, "end": v(0.52, -10.71) * mm});
            skLineSegment(sketch, "E800", {"start": v(0.52, -10.71) * mm, "end": v(0.56, -10.04) * mm});
            skLineSegment(sketch, "E801", {"start": v(3.74, -10.04) * mm, "end": v(5.9, -10.04) * mm});
            skLineSegment(sketch, "E802", {"start": v(5.9, -10.04) * mm, "end": v(5.92, -11.57) * mm});
            skLineSegment(sketch, "E803", {"start": v(5.92, -11.57) * mm, "end": v(5.87, -11.61) * mm});
            skLineSegment(sketch, "E804", {"start": v(5.87, -11.61) * mm, "end": v(5.82, -11.64) * mm});
            skLineSegment(sketch, "E805", {"start": v(5.82, -11.64) * mm, "end": v(5.77, -11.68) * mm});
            skLineSegment(sketch, "E806", {"start": v(5.77, -11.68) * mm, "end": v(5.71, -11.7) * mm});
            skLineSegment(sketch, "E807", {"start": v(5.71, -11.7) * mm, "end": v(5.66, -11.73) * mm});
            skLineSegment(sketch, "E808", {"start": v(5.66, -11.73) * mm, "end": v(5.6, -11.76) * mm});
            skLineSegment(sketch, "E809", {"start": v(5.6, -11.76) * mm, "end": v(5.55, -11.78) * mm});
            skLineSegment(sketch, "E810", {"start": v(5.55, -11.78) * mm, "end": v(5.5, -11.8) * mm});
            skLineSegment(sketch, "E811", {"start": v(5.5, -11.8) * mm, "end": v(5.43, -11.82) * mm});
            skLineSegment(sketch, "E812", {"start": v(5.43, -11.82) * mm, "end": v(5.38, -11.84) * mm});
            skLineSegment(sketch, "E813", {"start": v(5.38, -11.84) * mm, "end": v(5.32, -11.86) * mm});
            skLineSegment(sketch, "E814", {"start": v(5.32, -11.86) * mm, "end": v(5.26, -11.87) * mm});
            skLineSegment(sketch, "E815", {"start": v(5.26, -11.87) * mm, "end": v(5.2, -11.88) * mm});
            skLineSegment(sketch, "E816", {"start": v(5.2, -11.88) * mm, "end": v(5.14, -11.89) * mm});
            skLineSegment(sketch, "E817", {"start": v(5.14, -11.89) * mm, "end": v(5.08, -11.9) * mm});
            skLineSegment(sketch, "E818", {"start": v(5.08, -11.9) * mm, "end": v(5.02, -11.9) * mm});
            skLineSegment(sketch, "E819", {"start": v(5.02, -11.9) * mm, "end": v(4.96, -11.9) * mm});
            skLineSegment(sketch, "E820", {"start": v(4.96, -11.9) * mm, "end": v(4.9, -11.91) * mm});
            skLineSegment(sketch, "E821", {"start": v(4.9, -11.91) * mm, "end": v(4.84, -11.91) * mm});
            skLineSegment(sketch, "E822", {"start": v(4.84, -11.91) * mm, "end": v(4.78, -11.91) * mm});
            skLineSegment(sketch, "E823", {"start": v(4.78, -11.91) * mm, "end": v(4.72, -11.9) * mm});
            skLineSegment(sketch, "E824", {"start": v(4.72, -11.9) * mm, "end": v(4.65, -11.9) * mm});
            skLineSegment(sketch, "E825", {"start": v(4.65, -11.9) * mm, "end": v(4.6, -11.9) * mm});
            skLineSegment(sketch, "E826", {"start": v(4.6, -11.9) * mm, "end": v(4.53, -11.9) * mm});
            skLineSegment(sketch, "E827", {"start": v(4.53, -11.9) * mm, "end": v(4.47, -11.88) * mm});
            skLineSegment(sketch, "E828", {"start": v(4.47, -11.88) * mm, "end": v(4.41, -11.87) * mm});
            skLineSegment(sketch, "E829", {"start": v(4.41, -11.87) * mm, "end": v(4.35, -11.86) * mm});
            skLineSegment(sketch, "E830", {"start": v(4.35, -11.86) * mm, "end": v(4.3, -11.85) * mm});
            skLineSegment(sketch, "E831", {"start": v(4.3, -11.85) * mm, "end": v(4.24, -11.83) * mm});
            skLineSegment(sketch, "E832", {"start": v(4.24, -11.83) * mm, "end": v(3.98, -11.72) * mm});
            skLineSegment(sketch, "E833", {"start": v(3.98, -11.72) * mm, "end": v(3.92, -11.68) * mm});
            skLineSegment(sketch, "E834", {"start": v(3.92, -11.68) * mm, "end": v(3.89, -11.66) * mm});
            skLineSegment(sketch, "E835", {"start": v(3.89, -11.66) * mm, "end": v(3.86, -11.63) * mm});
            skLineSegment(sketch, "E836", {"start": v(3.86, -11.63) * mm, "end": v(3.83, -11.6) * mm});
            skLineSegment(sketch, "E837", {"start": v(3.83, -11.6) * mm, "end": v(3.82, -11.58) * mm});
            skLineSegment(sketch, "E838", {"start": v(3.82, -11.58) * mm, "end": v(3.81, -11.56) * mm});
            skLineSegment(sketch, "E839", {"start": v(3.81, -11.56) * mm, "end": v(3.8, -11.54) * mm});
            skLineSegment(sketch, "E840", {"start": v(3.8, -11.54) * mm, "end": v(3.8, -11.52) * mm});
            skLineSegment(sketch, "E841", {"start": v(3.8, -11.52) * mm, "end": v(3.79, -11.5) * mm});
            skLineSegment(sketch, "E842", {"start": v(3.79, -11.5) * mm, "end": v(3.78, -11.48) * mm});
            skLineSegment(sketch, "E843", {"start": v(3.78, -11.48) * mm, "end": v(3.78, -11.46) * mm});
            skLineSegment(sketch, "E844", {"start": v(3.78, -11.46) * mm, "end": v(3.74, -10.04) * mm});
            skSolve(sketch);
        }
        {
            var Q0;
            Q0=makeQuery(id+"F2.imprint","IMPRINT",FACE,{"disambiguationData":[TD([[makeQuery(id+"F2.imprint","IMPRINT",EDGE,{"derivedFrom":sQuery(id+"F2.wireOp",EDGE,"E1")}),-1.0]])]});
            var Q1;
            Q1=makeQuery(id+"F2.imprint","IMPRINT",FACE,{"disambiguationData":[TD([[makeQuery(id+"F2.imprint","IMPRINT",EDGE,{"derivedFrom":sQuery(id+"F2.wireOp",EDGE,"E365")}),-1.0]])]});
            var Q2;
            Q2=makeQuery(id+"F2.imprint","IMPRINT",FACE,{"disambiguationData":[TD([[makeQuery(id+"F2.imprint","IMPRINT",EDGE,{"derivedFrom":sQuery(id+"F2.wireOp",EDGE,"E441")}),-1.0]])]});
            var Q3;
            Q3=makeQuery(id+"F2.imprint","IMPRINT",FACE,{"disambiguationData":[TD([[makeQuery(id+"F2.imprint","IMPRINT",EDGE,{"derivedFrom":sQuery(id+"F2.wireOp",EDGE,"E521")}),-1.0]])]});
            var Q4;
            Q4=makeQuery(id+"F2.imprint","IMPRINT",FACE,{"disambiguationData":[TD([[makeQuery(id+"F2.imprint","IMPRINT",EDGE,{"derivedFrom":sQuery(id+"F2.wireOp",EDGE,"E609")}),-1.0]])]});
            var Q5;
            Q5=makeQuery(id+"F2.imprint","IMPRINT",FACE,{"disambiguationData":[TD([[makeQuery(id+"F2.imprint","IMPRINT",EDGE,{"derivedFrom":sQuery(id+"F2.wireOp",EDGE,"E801")}),-1.0]])]});
            var Q6;
            Q6=makeQuery(id+"F2.imprint","IMPRINT",FACE,{"disambiguationData":[TD([[makeQuery(id+"F2.imprint","IMPRINT",EDGE,{"derivedFrom":sQuery(id+"F2.wireOp",EDGE,"E745")}),-1.0]])]});
            var Q7;
            Q7=makeQuery(id+"F2.imprint","IMPRINT",FACE,{"disambiguationData":[TD([[makeQuery(id+"F2.imprint","IMPRINT",EDGE,{"derivedFrom":sQuery(id+"F2.wireOp",EDGE,"E696")}),-1.0]])]});
            var Q8;
            Q8=makeQuery(id+"F2.imprint","IMPRINT",FACE,{"disambiguationData":[TD([[makeQuery(id+"F2.imprint","IMPRINT",EDGE,{"derivedFrom":sQuery(id+"F2.wireOp",EDGE,"E650")}),-1.0]])]});
            var Q9;
            Q9=makeQuery(id+"F2.imprint","IMPRINT",FACE,{"disambiguationData":[TD([[makeQuery(id+"F2.imprint","IMPRINT",EDGE,{"derivedFrom":sQuery(id+"F2.wireOp",EDGE,"E555")}),-1.0]])]});
            var Q10;
            Q10=makeQuery(id+"F2.imprint","IMPRINT",FACE,{"disambiguationData":[TD([[makeQuery(id+"F2.imprint","IMPRINT",EDGE,{"derivedFrom":sQuery(id+"F2.wireOp",EDGE,"E472")}),-1.0]])]});
            var Q11;
            Q11=makeQuery(id+"F2.imprint","IMPRINT",FACE,{"disambiguationData":[TD([[makeQuery(id+"F2.imprint","IMPRINT",EDGE,{"derivedFrom":sQuery(id+"F2.wireOp",EDGE,"E410")}),-1.0]])]});
            var Q12;
            Q12=makeQuery(id+"F2.imprint","IMPRINT",FACE,{"disambiguationData":[TD([[makeQuery(id+"F2.imprint","IMPRINT",EDGE,{"derivedFrom":sQuery(id+"F2.wireOp",EDGE,"E321")}),-1.0]])]});
            extrude(context, id + "F3", {"entities" : qUnion([Q0, Q1, Q2, Q3, Q4, Q5, Q6, Q7, Q8, Q9, Q10, Q11, Q12]), "operationType" : NewBodyOperationType.ADD, "depth" : 4 * mm});
        }
    });
